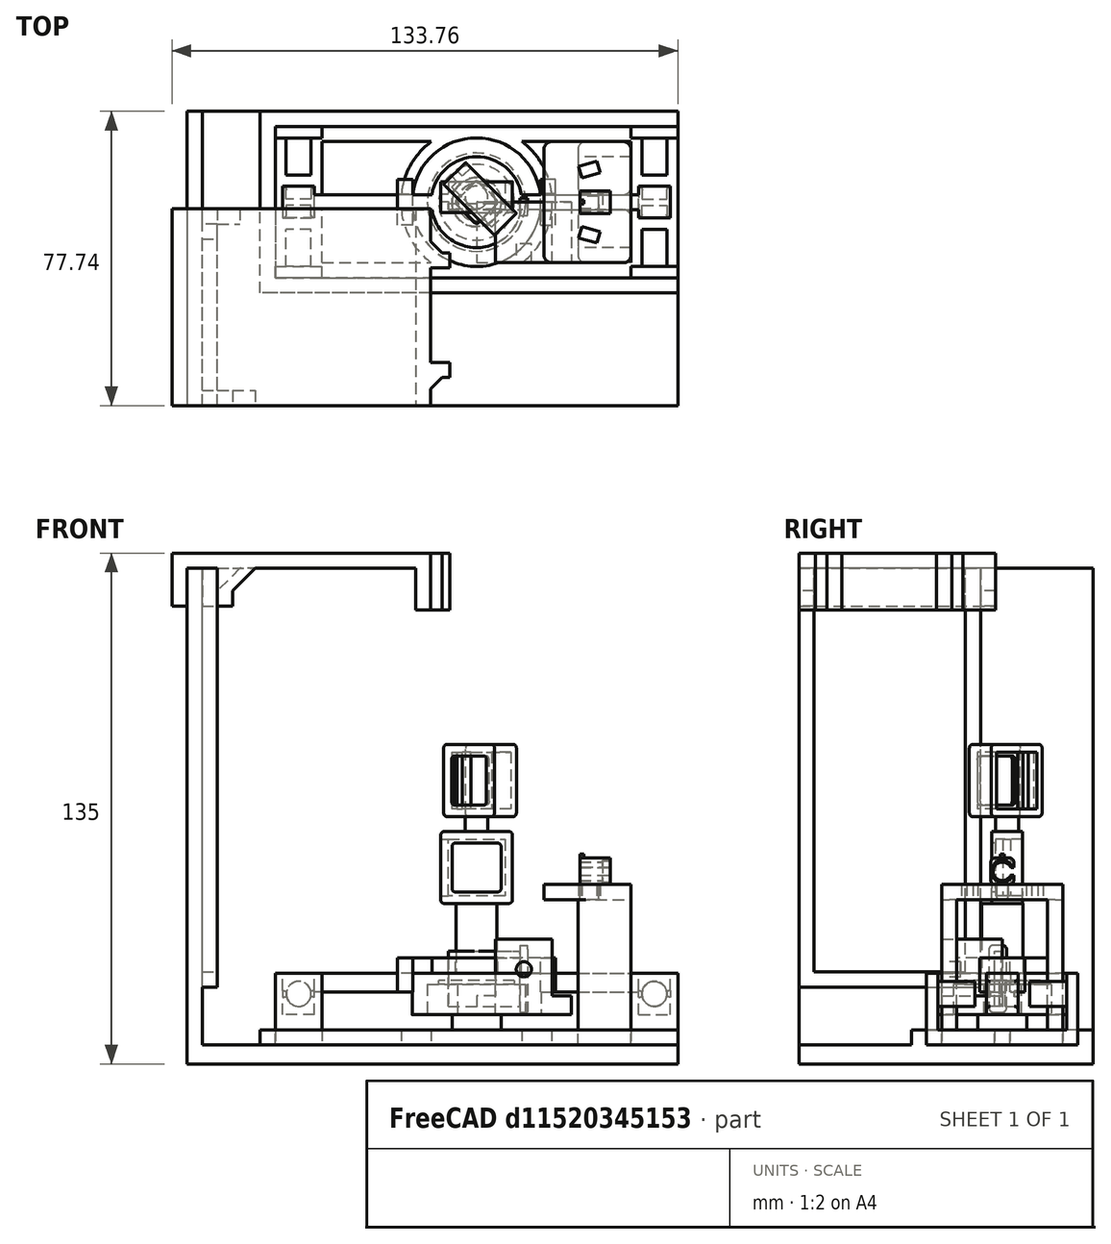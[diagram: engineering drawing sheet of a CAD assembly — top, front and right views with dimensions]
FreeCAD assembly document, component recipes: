
FREECAD ASSEMBLY — COMPONENT RECIPES ("laser2")

This assembly document has 16 components, labeled P0..P15 below (a component is one placed body or linked part). 16 of them carry a construction recipe — the FreeCAD feature program that regenerates the part from scratch, quoted from this document or its linked companion documents; the rest are supplied as boundary geometry only. No exploded tour is included for this assembly.
COMPONENT P0 — recipe-attached ("stator", modeled in this document).
Construction recipe (the document's own serialized feature program — sketch geometry with constraints, then the solid features built on it; lengths are millimeters unless a unit is written):

FEATURE [PartDesign::SubShapeBinder] Binder
  BindCopyOnChange = 0
  BindMode = 0
  ClaimChildren = false
  Context = -> Body [Boolean.Body001.Binder.]
  Fuse = false
  MakeFace = true
  OffsetFill = false
  OffsetIntersection = false
  OffsetJoinType = 0
  OffsetOpenResult = false
  PartialLoad = false
  Refine = true
  Relative = true
  Support = -> [Body002]
  _Version = 2
FEATURE [Sketcher::SketchObject] Sketch001
  ArcFitTolerance = 1e-06
  AttachmentSupport = -> [Origin002]
  ExternalGeometry = -> [Binder]
  ExternalTypes = [0]
  FullyConstrained = true
  MakeInternals = false
  MapMode = 5
  sketch-geometry (1):
    g0: Circle CenterX=0 CenterY=0 CenterZ=0 NormalX=0 NormalY=0 NormalZ=1 AngleXU=0 Radius=5
  constraints (2):
    c: Coincident(g0,g-1)
    c: Equal(g-3,g0)
FEATURE [PartDesign::Pad] Pad
  Direction = (0,0,1)
  Length = 8
  Length2 = 10
  Profile = -> Sketch001
  ReferenceAxis = -> Sketch001 [N_Axis]
  Refine = true
  SideType = 0
  Suppressed = false
  Type = 0
  Type2 = 0
  expr: Length = VarSet.bearing_height
FEATURE [Sketcher::SketchObject] Sketch020
  ArcFitTolerance = 1e-06
  AttachmentSupport = -> [Pad]
  ExternalGeometry = -> [Pad]
  ExternalTypes = [0]
  FullyConstrained = true
  MakeInternals = false
  MapMode = 5
  Placement = pos=(0,0,0) rot=(1,0,0;3.14159rad)
  sketch-geometry (1):
    g0: Circle CenterX=0 CenterY=0 CenterZ=0 NormalX=0 NormalY=0 NormalZ=1 AngleXU=0 Radius=6.5
  constraints (2):
    c: Coincident(g0,g-3)
    c: Distance(g-3,g0) = 1.5
FEATURE [PartDesign::Pad] Pad012
  BaseFeature = -> Pad
  Direction = (0,0,-1)
  Length = 4
  Length2 = 10
  Profile = -> Sketch020
  ReferenceAxis = -> Sketch020 [N_Axis]
  Refine = true
  SideType = 0
  Suppressed = false
  Type = 0
  Type2 = 0
FEATURE [PartDesign::Body] Body001  label="stator"
  AllowCompound = false
  Group = -> [Sketch001,Pad,Binder,Sketch020,Pad012]
  Origin = -> Origin002
  Tip = -> Pad012
COMPONENT P1 — recipe-attached ("mirror_base", modeled in this document).
Construction recipe (the document's own serialized feature program — sketch geometry with constraints, then the solid features built on it; lengths are millimeters unless a unit is written):

FEATURE [PartDesign::SubShapeBinder] Binder006
  BindCopyOnChange = 0
  BindMode = 0
  ClaimChildren = false
  Context = -> Body005 [Binder006.]
  Fuse = false
  MakeFace = true
  OffsetFill = false
  OffsetIntersection = false
  OffsetJoinType = 0
  OffsetOpenResult = false
  PartialLoad = false
  Refine = true
  Relative = true
  Support = -> [Body004]
  _Version = 2
FEATURE [Sketcher::SketchObject] Sketch031
  ArcFitTolerance = 1e-06
  AttachmentSupport = -> [Binder006]
  ExternalGeometry = -> [Binder006]
  ExternalTypes = [0,0,0,0,0,0,0,0]
  FullyConstrained = true
  MakeInternals = false
  MapMode = 5
  Placement = pos=(0,0,11) rot=(1,0,0;3.14159rad)
  sketch-geometry (16):
    g0: ArcOfCircle CenterX=-4.58579 CenterY=1.3e-15 CenterZ=0 NormalX=0 NormalY=0 NormalZ=1 AngleXU=-1.5708 Radius=0.85 StartAngle=3.92699 EndAngle=5.49779
    g1: LineSegment StartX=-5.18683 StartY=-0.601041 StartZ=0 EndX=-0.601041 EndY=-5.18683 EndZ=0
    g2: ArcOfCircle CenterX=-1.2e-15 CenterY=-4.58579 CenterZ=0 NormalX=0 NormalY=0 NormalZ=1 AngleXU=-1.5708 Radius=0.85 StartAngle=5.49779 EndAngle=7.06858
    g3: LineSegment StartX=0.601041 StartY=-5.18683 StartZ=0 EndX=5.18683 EndY=-0.601041 EndZ=0
    g4: ArcOfCircle CenterX=4.58579 CenterY=-7e-16 CenterZ=0 NormalX=0 NormalY=0 NormalZ=1 AngleXU=-1.5708 Radius=0.85 StartAngle=0.785398 EndAngle=2.35619
    g5: LineSegment StartX=5.18683 StartY=0.601041 StartZ=0 EndX=0.601041 EndY=5.18683 EndZ=0
    g6: ArcOfCircle CenterX=3e-16 CenterY=4.58579 CenterZ=0 NormalX=0 NormalY=0 NormalZ=1 AngleXU=-1.5708 Radius=0.85 StartAngle=2.35619 EndAngle=3.92699
    g7: LineSegment StartX=-0.601041 StartY=5.18683 StartZ=0 EndX=-5.18683 EndY=0.601041 EndZ=0
    g8: LineSegment [constr] StartX=5.18683 StartY=0.601041 StartZ=0 EndX=4.58579 EndY=-7e-16 EndZ=0
    g9: LineSegment [constr] StartX=4.58579 StartY=-7e-16 StartZ=0 EndX=5.18683 EndY=-0.601041 EndZ=0
    g10: LineSegment [constr] StartX=0.601041 StartY=5.18683 StartZ=0 EndX=3e-16 EndY=4.58579 EndZ=0
    g11: LineSegment [constr] StartX=3e-16 StartY=4.58579 StartZ=0 EndX=-0.601041 EndY=5.18683 EndZ=0
    g12: LineSegment [constr] StartX=-5.18683 StartY=0.601041 StartZ=0 EndX=-4.58579 EndY=1.3e-15 EndZ=0
    g13: LineSegment [constr] StartX=-4.58579 StartY=1.3e-15 StartZ=0 EndX=-5.18683 EndY=-0.601041 EndZ=0
    g14: LineSegment [constr] StartX=-0.601041 StartY=-5.18683 StartZ=0 EndX=-1.1e-15 EndY=-4.58579 EndZ=0
    g15: LineSegment [constr] StartX=-1.2e-15 StartY=-4.58579 StartZ=0 EndX=0.601041 EndY=-5.18683 EndZ=0
  constraints (33):
    c: Tangent(g0,g1) = -1.5708
    c: Tangent(g0,g7) = -1.5708
    c: Tangent(g1,g2) = -1.5708
    c: Tangent(g2,g3) = -1.5708
    c: Tangent(g3,g4) = -1.5708
    c: Tangent(g4,g5) = -1.5708
    c: Tangent(g5,g6) = -1.5708
    c: Tangent(g6,g7) = -1.5708
    c: Coincident(g8,g4)
    c: Coincident(g8,g4)
    c: Coincident(g9,g4)
    c: Coincident(g9,g3)
    c: Perpendicular(g8,g9)
    c: Coincident(g10,g5)
    c: Coincident(g10,g6)
    c: Coincident(g11,g6)
    c: Coincident(g11,g6)
    c: Distance(g11,g11) = 0.85
    c: Perpendicular(g10,g11)
    c: Coincident(g12,g0)
    c: Coincident(g12,g0)
    c: Coincident(g13,g0)
    c: Coincident(g13,g0)
    c: Perpendicular(g12,g13)
    c: Distance(g12,g12) = 0.85
    c: Coincident(g14,g1)
    c: Coincident(g14,g2)
    c: Coincident(g15,g2)
    c: Coincident(g15,g2)
    c: Distance(g15,g15) = 0.85
    c: Coincident(g0,g-10)
    c: Coincident(g6,g-5)
    c: Coincident(g4,g-6)
FEATURE [PartDesign::Pad] Pad021
  Direction = (0,0,-1)
  Length = 18.4
  Length2 = 10
  Offset = 16
  Profile = -> Sketch031
  ReferenceAxis = -> Sketch031 [N_Axis]
  Refine = true
  Reversed = true
  SideType = 0
  Suppressed = false
  Type = 0
  Type2 = 0
FEATURE [PartDesign::Body] Body005  label="mirror_base"
  AllowCompound = false
  Group = -> [Sketch031,Binder006,Pad021]
  Origin = -> Origin011
  Placement = pos=(0,0,0) rot=(0,0,1;-1.5708rad)
  Tip = -> Pad021
COMPONENT P2 — recipe-attached ("cover", modeled in this document).
Construction recipe (the document's own serialized feature program — sketch geometry with constraints, then the solid features built on it; lengths are millimeters unless a unit is written):

FEATURE [PartDesign::SubShapeBinder] Binder011
  BindCopyOnChange = 0
  BindMode = 0
  ClaimChildren = false
  Context = -> Body006 [Binder011.]
  Fuse = false
  MakeFace = true
  OffsetFill = false
  OffsetIntersection = false
  OffsetJoinType = 0
  OffsetOpenResult = false
  PartialLoad = false
  Refine = true
  Relative = true
  Support = -> [Body008]
  _Version = 2
FEATURE [Sketcher::SketchObject] Sketch036
  ArcFitTolerance = 1e-06
  AttachmentSupport = -> [Binder011]
  ExternalGeometry = -> [Binder011]
  ExternalTypes = [0,0,0,0]
  FullyConstrained = true
  MakeInternals = false
  MapMode = 5
  Placement = pos=(-7.5,0,0) rot=(0.57735,0.57735,0.57735;2.0944rad)
  sketch-geometry (6):
    g0: LineSegment StartX=-1.98579 StartY=16.8 StartZ=0 EndX=-1.98579 EndY=2.2 EndZ=0
    g1: LineSegment StartX=-1.98579 StartY=2.2 StartZ=0 EndX=-0.385786 EndY=2.2 EndZ=0
    g2: LineSegment StartX=-0.385786 StartY=2.2 StartZ=0 EndX=-0.385786 EndY=16.8 EndZ=0
    g3: LineSegment StartX=-0.385786 StartY=16.8 StartZ=0 EndX=-1.98579 EndY=16.8 EndZ=0
    g4: LineSegment [constr] StartX=-0.185786 StartY=2 StartZ=0 EndX=-2.18579 EndY=17 EndZ=0
    g5: GeomPoint [constr] X=-1.18579 Y=9.5 Z=0
  constraints (14):
    c: Coincident(g0,g1)
    c: Coincident(g1,g2)
    c: Coincident(g2,g3)
    c: Coincident(g3,g0)
    c: Vertical(g0)
    c: Vertical(g2)
    c: Horizontal(g1)
    c: Horizontal(g3)
    c: Coincident(g4,g-6)
    c: Coincident(g4,g-4)
    c: Symmetric(g4,g4,g5)
    c: Symmetric(g2,g0,g5)
    c: Distance(g-3,g3) = 0.2
    c: Distance(g-5,g2) = 0.2
FEATURE [PartDesign::Pad] Pad024
  Direction = (1,0,0)
  Length = 10
  Length2 = 10
  Offset = -2
  Profile = -> Sketch036
  ReferenceAxis = -> Sketch036 [N_Axis]
  Refine = true
  SideType = 0
  Suppressed = false
  Type = 3
  Type2 = 0
  UpToFace = -> Binder011 [Face6]
FEATURE [Sketcher::SketchObject] Sketch037
  ArcFitTolerance = 1e-06
  AttachmentSupport = -> [Pad024]
  ExternalGeometry = -> [Pad024]
  ExternalTypes = [0]
  FullyConstrained = true
  MakeInternals = false
  MapMode = 5
  Placement = pos=(11.5,0,0) rot=(0.57735,0.57735,0.57735;2.0944rad)
  sketch-geometry (6):
    g0: LineSegment StartX=-3.48579 StartY=18.3 StartZ=0 EndX=-3.48579 EndY=0.7 EndZ=0
    g1: LineSegment StartX=-3.48579 StartY=0.7 StartZ=0 EndX=1.11421 EndY=0.7 EndZ=0
    g2: LineSegment StartX=1.11421 StartY=0.7 StartZ=0 EndX=1.11421 EndY=18.3 EndZ=0
    g3: LineSegment StartX=1.11421 StartY=18.3 StartZ=0 EndX=-3.48579 EndY=18.3 EndZ=0
    g4: LineSegment [constr] StartX=-1.98579 StartY=16.8 StartZ=0 EndX=-0.385786 EndY=2.2 EndZ=0
    g5: GeomPoint [constr] X=-1.18579 Y=9.5 Z=0
  constraints (14):
    c: Coincident(g0,g1)
    c: Coincident(g1,g2)
    c: Coincident(g2,g3)
    c: Coincident(g3,g0)
    c: Vertical(g0)
    c: Vertical(g2)
    c: Horizontal(g1)
    c: Horizontal(g3)
    c: Coincident(g4,g-6)
    c: Coincident(g4,g-4)
    c: Symmetric(g4,g4,g5)
    c: Symmetric(g0,g2,g5)
    c: Distance(g3,g-5) = 1.5
    c: Distance(g2,g-4) = 1.5
FEATURE [PartDesign::Pad] Pad025
  BaseFeature = -> Pad024
  Direction = (1,0,0)
  Length = 2
  Length2 = 10
  Profile = -> Sketch037
  ReferenceAxis = -> Sketch037 [N_Axis]
  Refine = true
  SideType = 0
  Suppressed = false
  Type = 0
  Type2 = 0
FEATURE [PartDesign::Fillet] Fillet003
  Base = -> Pad025 [Edge17,Edge20,Edge18,Edge22]
  BaseFeature = -> Pad025
  Radius = 1
  Refine = true
  SupportTransform = false
  Suppressed = false
  UseAllEdges = false
FEATURE [PartDesign::Body] Body006  label="cover"
  AllowCompound = false
  Group = -> [Binder011,Sketch036,Pad024,Sketch037,Pad025,Fillet003]
  Origin = -> Origin013
  Tip = -> Fillet003
COMPONENT P3 — recipe-attached ("mirror", modeled in this document).
Construction recipe (the document's own serialized feature program — sketch geometry with constraints, then the solid features built on it; lengths are millimeters unless a unit is written):

FEATURE [Sketcher::SketchObject] Sketch044
  ArcFitTolerance = 1e-06
  AttachmentSupport = -> [Origin019]
  ExternalTypes = [0]
  FullyConstrained = true
  MakeInternals = false
  MapMode = 5
  expr: Constraints[14] = 1 mm + 1.8 mm
  expr: Constraints[8] = VarSet.mirror_width + 2 * 2 mm
  sketch-geometry (7):
    g0: LineSegment StartX=-9.5 StartY=2.8 StartZ=0 EndX=-9.5 EndY=-5.38579 EndZ=0
    g1: LineSegment StartX=-9.5 StartY=-5.38579 StartZ=0 EndX=9.5 EndY=-5.38579 EndZ=0
    g2: LineSegment StartX=9.5 StartY=-5.38579 StartZ=0 EndX=9.5 EndY=2.8 EndZ=0
    g3: LineSegment StartX=9.5 StartY=2.8 StartZ=0 EndX=-9.5 EndY=2.8 EndZ=0
    g4: LineSegment [constr] StartX=-9.5 StartY=-5.38579 StartZ=0 EndX=0 EndY=0 EndZ=0
    g5: LineSegment [constr] StartX=0 StartY=0 StartZ=0 EndX=9.5 EndY=-5.38579 EndZ=0
    g6: GeomPoint [constr] X=0 Y=-5.38579 Z=0
  constraints (18):
    c: Coincident(g0,g1)
    c: Coincident(g1,g2)
    c: Coincident(g2,g3)
    c: Coincident(g3,g0)
    c: Vertical(g0)
    c: Vertical(g2)
    c: Horizontal(g1)
    c: Horizontal(g3)
    c: Distance(g3,g3) = 19
    c: Coincident(g4,g0)
    c: Coincident(g4,g-1)
    c: Coincident(g5,g4)
    c: Coincident(g5,g1)
    c: Equal(g5,g4)
    c: Distance(g4,g3) = 2.8
    c: PointOnObject(g6,g-3)
    c: PointOnObject(g6,g1)
    c: PointOnObject(g6,g-2)
FEATURE [PartDesign::Pad] Pad031
  Direction = (0,0,1)
  Length = 19
  Length2 = 10
  Profile = -> Sketch044
  ReferenceAxis = -> Sketch044 [N_Axis]
  Refine = true
  SideType = 0
  Suppressed = false
  Type = 0
  Type2 = 0
  expr: Length = 2 * 2 mm + VarSet.mirror_width
FEATURE [Sketcher::SketchObject] Sketch045
  ArcFitTolerance = 1e-06
  AttachmentSupport = -> [Pad031]
  ExternalGeometry = -> [Pad031]
  ExternalTypes = [0,0,0,0]
  FullyConstrained = true
  MakeInternals = false
  MapMode = 5
  Placement = pos=(0,-5.38579,0) rot=(1,0,0;1.5708rad)
  sketch-geometry (10):
    g0: LineSegment StartX=-7.5 StartY=17 StartZ=0 EndX=-7.5 EndY=2 EndZ=0
    g1: LineSegment StartX=-7.5 StartY=2 StartZ=0 EndX=7.5 EndY=2 EndZ=0
    g2: LineSegment StartX=7.5 StartY=2 StartZ=0 EndX=7.5 EndY=17 EndZ=0
    g3: LineSegment StartX=7.5 StartY=17 StartZ=0 EndX=-7.5 EndY=17 EndZ=0
    g4: LineSegment StartX=-6.5 StartY=16 StartZ=0 EndX=-6.5 EndY=3 EndZ=0
    g5: LineSegment StartX=-6.5 StartY=3 StartZ=0 EndX=6.5 EndY=3 EndZ=0
    g6: LineSegment StartX=6.5 StartY=3 StartZ=0 EndX=6.5 EndY=16 EndZ=0
    g7: LineSegment StartX=6.5 StartY=16 StartZ=0 EndX=-6.5 EndY=16 EndZ=0
    g8: LineSegment [constr] StartX=9.5 StartY=0 StartZ=0 EndX=-9.5 EndY=19 EndZ=0
    g9: GeomPoint [constr] X=2.45925e-11 Y=9.5 Z=0
  constraints (25):
    c: Coincident(g0,g1)
    c: Coincident(g1,g2)
    c: Coincident(g2,g3)
    c: Coincident(g3,g0)
    c: Vertical(g0)
    c: Vertical(g2)
    c: Horizontal(g1)
    c: Horizontal(g3)
    c: Coincident(g4,g5)
    c: Coincident(g5,g6)
    c: Coincident(g6,g7)
    c: Coincident(g7,g4)
    c: Vertical(g4)
    c: Vertical(g6)
    c: Horizontal(g5)
    c: Horizontal(g7)
    c: Coincident(g8,g-6)
    c: Coincident(g8,g-4)
    c: Symmetric(g8,g8,g9)
    c: Symmetric(g0,g1,g9)
    c: Symmetric(g4,g6,g9)
    c: Distance(g4,g0) = 1
    c: Distance(g-4,g0) = 2
    c: PointOnObject(g0,g8)
    c: PointOnObject(g4,g8)
FEATURE [PartDesign::Pocket] Pocket007
  BaseFeature = -> Pad031
  Direction = (0,1,-2e-16)
  Length = 7.2
  Length2 = 5
  Profile = -> Sketch045 [Edge1,Edge4,Edge3,Edge2]
  ReferenceAxis = -> Sketch045 [N_Axis]
  Refine = true
  SideType = 0
  Suppressed = false
  Type = 0
  Type2 = 0
  expr: Length = 5 mm + 2.2 mm
FEATURE [PartDesign::Pocket] Pocket008
  BaseFeature = -> Pocket007
  Direction = (0,1,-2e-16)
  Length = 5
  Length2 = 5
  Profile = -> Sketch045 [Edge5,Edge8,Edge7,Edge6]
  ReferenceAxis = -> Sketch045 [N_Axis]
  Refine = true
  SideType = 0
  Suppressed = false
  Type = 1
  Type2 = 0
FEATURE [Sketcher::SketchObject] Sketch046
  ArcFitTolerance = 1e-06
  AttachmentSupport = -> [Pocket008]
  ExternalGeometry = -> [Pocket008]
  ExternalTypes = [0]
  FullyConstrained = true
  MakeInternals = false
  MapMode = 5
  Placement = pos=(9.5,0,0) rot=(0.57735,0.57735,0.57735;2.0944rad)
  sketch-geometry (6):
    g0: LineSegment StartX=-0.185786 StartY=17 StartZ=0 EndX=-2.18579 EndY=17 EndZ=0
    g1: LineSegment StartX=-2.18579 StartY=17 StartZ=0 EndX=-2.18579 EndY=2 EndZ=0
    g2: LineSegment StartX=-2.18579 StartY=2 StartZ=0 EndX=-0.185786 EndY=2 EndZ=0
    g3: LineSegment StartX=-0.185786 StartY=17 StartZ=0 EndX=-0.185786 EndY=2 EndZ=0
    g4: LineSegment [constr] StartX=-0.185786 StartY=17 StartZ=0 EndX=1.81421 EndY=17 EndZ=0
    g5: LineSegment [constr] StartX=-0.185786 StartY=2 StartZ=0 EndX=1.81421 EndY=2 EndZ=0
  constraints (16):
    c: Coincident(g0,g1)
    c: Coincident(g1,g2)
    c: Horizontal(g0)
    c: Horizontal(g2)
    c: Vertical(g1)
    c: Distance(g2,g2) = 2
    c: Coincident(g3,g0)
    c: Coincident(g3,g2)
    c: Vertical(g3)
    c: Coincident(g4,g0)
    c: Coincident(g5,g2)
    c: Horizontal(g5)
    c: Horizontal(g4)
    c: Distance(g5,g5) = 2
    c: Coincident(g5,g-3)
    c: Coincident(g4,g-3)
FEATURE [PartDesign::Pocket] Pocket009
  BaseFeature = -> Pocket008
  Direction = (-1,0,0)
  Length = 5
  Length2 = 5
  Profile = -> Sketch046
  ReferenceAxis = -> Sketch046 [N_Axis]
  Refine = true
  SideType = 0
  Suppressed = false
  Type = 2
  Type2 = 0
FEATURE [PartDesign::Fillet] Fillet006
  Base = -> Pocket009 [Edge4,Edge20,Edge19,Edge3,Edge26,Edge27,Edge31,Edge29]
  BaseFeature = -> Pocket009
  Radius = 1
  Refine = true
  SupportTransform = false
  Suppressed = false
  UseAllEdges = false
FEATURE [PartDesign::Body] Body008  label="mirror"
  AllowCompound = false
  Group = -> [Sketch044,Sketch045,Sketch046,Pad031,Pocket007,Pocket008,Pocket009,Fillet006]
  Origin = -> Origin019
  Tip = -> Fillet006
COMPONENT P4 — recipe-attached ("container", modeled in this document).
Construction recipe (the document's own serialized feature program — sketch geometry with constraints, then the solid features built on it; lengths are millimeters unless a unit is written):

FEATURE [PartDesign::SubShapeBinder] Binder014
  BindCopyOnChange = 0
  BindMode = 0
  ClaimChildren = false
  Context = -> Body009 [Binder014.]
  Fuse = false
  MakeFace = true
  OffsetFill = false
  OffsetIntersection = false
  OffsetJoinType = 0
  OffsetOpenResult = false
  PartialLoad = false
  Refine = true
  Relative = true
  Support = -> [Assembly002]
  _Version = 2
FEATURE [Sketcher::SketchObject] Sketch047
  ArcFitTolerance = 1e-06
  AttachmentOffset = pos=(0,0,0) rot=(0,0,1;1.5708rad)
  AttachmentSupport = -> [Binder014]
  ExternalGeometry = -> [Binder014]
  ExternalTypes = [0,0,0,0,0]
  FullyConstrained = true
  MakeInternals = false
  MapMode = 45
  Placement = pos=(1.32e-14,-2.28733e-11,-8) rot=(0,0,1;3.14159rad)
  sketch-geometry (4):
    g0: LineSegment StartX=76.5314 StartY=53.7373 StartZ=0 EndX=-53.2307 EndY=53.7373 EndZ=0
    g1: LineSegment StartX=-53.2307 StartY=53.7373 StartZ=0 EndX=-53.2307 EndY=-24 EndZ=0
    g2: LineSegment StartX=-53.2307 StartY=-24 StartZ=0 EndX=76.5314 EndY=-24 EndZ=0
    g3: LineSegment StartX=76.5314 StartY=-24 StartZ=0 EndX=76.5314 EndY=53.7373 EndZ=0
  constraints (12):
    c: Coincident(g0,g1)
    c: Coincident(g1,g2)
    c: Coincident(g2,g3)
    c: Coincident(g3,g0)
    c: Horizontal(g0)
    c: Horizontal(g2)
    c: Vertical(g1)
    c: Vertical(g3)
    c: Distance(g-5,g0) = 4
    c: Distance(g-5,g3) = 4
    c: PointOnObject(g-7,g1)
    c: Distance(g-7,g1) = 4
FEATURE [PartDesign::Pad] Pad032
  Direction = (0,0,1)
  Length = 5
  Length2 = 10
  Profile = -> Sketch047
  ReferenceAxis = -> Sketch047 [N_Axis]
  Refine = true
  Reversed = true
  SideType = 0
  Suppressed = false
  Type = 0
  Type2 = 0
FEATURE [Sketcher::SketchObject] Sketch048
  ArcFitTolerance = 1e-06
  AttachmentSupport = -> [Pad032]
  ExternalGeometry = -> [Pad032,Binder014]
  ExternalTypes = [0,0]
  FullyConstrained = true
  MakeInternals = false
  MapMode = 5
  Placement = pos=(0,0,-8) rot=(0,0,1;0rad)
  sketch-geometry (4):
    g0: LineSegment StartX=-76.5314 StartY=24 StartZ=0 EndX=-76.5314 EndY=-53.7373 EndZ=0
    g1: LineSegment StartX=-76.5314 StartY=-53.7373 StartZ=0 EndX=-72.5314 EndY=-53.7373 EndZ=0
    g2: LineSegment StartX=-72.5314 StartY=-53.7373 StartZ=0 EndX=-72.5314 EndY=24 EndZ=0
    g3: LineSegment StartX=-72.5314 StartY=24 StartZ=0 EndX=-76.5314 EndY=24 EndZ=0
  constraints (10):
    c: Coincident(g0,g1)
    c: Coincident(g1,g2)
    c: Coincident(g2,g3)
    c: Coincident(g3,g0)
    c: Vertical(g2)
    c: Horizontal(g1)
    c: Horizontal(g3)
    c: Coincident(g0,g-3)
    c: Coincident(g0,g-3)
    c: PointOnObject(g-4,g2)
FEATURE [PartDesign::Pad] Pad033
  BaseFeature = -> Pad032
  Direction = (0,0,1)
  Length = 126
  Length2 = 10
  Profile = -> Sketch048
  ReferenceAxis = -> Sketch048 [N_Axis]
  Refine = true
  SideType = 0
  Suppressed = false
  Type = 0
  Type2 = 0
FEATURE [Sketcher::SketchObject] Sketch049
  ArcFitTolerance = 1e-06
  AttachmentSupport = -> [Pad033]
  ExternalGeometry = -> [Binder014,Pad033]
  ExternalTypes = [0,0,0,0,0]
  FullyConstrained = true
  MakeInternals = false
  MapMode = 5
  Placement = pos=(0,0,-8) rot=(0,0,1;0rad)
  sketch-geometry (8):
    g0: LineSegment StartX=53.2307 StartY=24 StartZ=0 EndX=-57.2307 EndY=24 EndZ=0
    g1: LineSegment StartX=53.2307 StartY=20 StartZ=0 EndX=-53.2307 EndY=20 EndZ=0
    g2: LineSegment StartX=53.2307 StartY=20 StartZ=0 EndX=53.2307 EndY=24 EndZ=0
    g3: LineSegment StartX=-53.2307 StartY=20 StartZ=0 EndX=-53.2307 EndY=-20 EndZ=0
    g4: LineSegment StartX=-53.2307 StartY=-20 StartZ=0 EndX=53.2307 EndY=-20 EndZ=0
    g5: LineSegment StartX=53.2307 StartY=-20 StartZ=0 EndX=53.2307 EndY=-24 EndZ=0
    g6: LineSegment StartX=53.2307 StartY=-24 StartZ=0 EndX=-57.2307 EndY=-24 EndZ=0
    g7: LineSegment StartX=-57.2307 StartY=-24 StartZ=0 EndX=-57.2307 EndY=24 EndZ=0
  constraints (19):
    c: Coincident(g0,g-7)
    c: PointOnObject(g0,g-7)
    c: Coincident(g1,g-5)
    c: Coincident(g1,g-6)
    c: Coincident(g2,g1)
    c: Coincident(g2,g0)
    c: Coincident(g3,g1)
    c: Coincident(g3,g-3)
    c: Coincident(g4,g3)
    c: Coincident(g4,g-4)
    c: Coincident(g5,g4)
    c: Vertical(g5)
    c: Coincident(g6,g5)
    c: Horizontal(g6)
    c: Coincident(g7,g6)
    c: Coincident(g7,g0)
    c: Vertical(g7)
    c: Distance(g1,g7) = 4
    c: Distance(g3,g6) = 4
FEATURE [PartDesign::Pad] Pad034
  BaseFeature = -> Pad033
  Direction = (0,0,1)
  Length = 4
  Length2 = 10
  Profile = -> Sketch049
  ReferenceAxis = -> Sketch049 [N_Axis]
  Refine = true
  SideType = 0
  Suppressed = false
  Type = 0
  Type2 = 0
FEATURE [Sketcher::SketchObject] Sketch050
  ArcFitTolerance = 1e-06
  AttachmentSupport = -> [Pad034]
  ExternalGeometry = -> [Pad034,Binder014]
  ExternalTypes = [0,0,0,0,0]
  FullyConstrained = true
  MakeInternals = false
  MapMode = 5
  Placement = pos=(-72.5314,0,0) rot=(0.57735,0.57735,0.57735;2.0944rad)
  sketch-geometry (10):
    g0: LineSegment [constr] StartX=-49.7373 StartY=117.762 StartZ=0 EndX=-49.7373 EndY=118 EndZ=0
    g1: LineSegment [constr] StartX=-9.73726 StartY=117.762 StartZ=0 EndX=-9.73726 EndY=118 EndZ=0
    g2: LineSegment StartX=-49.7373 StartY=118 StartZ=0 EndX=-53.7373 EndY=118 EndZ=0
    g3: LineSegment StartX=-53.7373 StartY=118 StartZ=0 EndX=-53.7373 EndY=7.30072 EndZ=0
    g4: LineSegment StartX=-49.7373 StartY=11.3007 StartZ=0 EndX=-49.7373 EndY=118 EndZ=0
    g5: LineSegment StartX=-49.7373 StartY=11.3007 StartZ=0 EndX=-9.73726 EndY=11.3007 EndZ=0
    g6: LineSegment StartX=-9.73726 StartY=11.3007 StartZ=0 EndX=-9.73726 EndY=118 EndZ=0
    g7: LineSegment StartX=-53.7373 StartY=7.30072 StartZ=0 EndX=-5.73726 EndY=7.30072 EndZ=0
    g8: LineSegment StartX=-5.73726 StartY=7.30072 StartZ=0 EndX=-5.73726 EndY=118 EndZ=0
    g9: LineSegment StartX=-9.73726 StartY=118 StartZ=0 EndX=-5.73726 EndY=118 EndZ=0
  constraints (25):
    c: Coincident(g0,g-4)
    c: PointOnObject(g0,g-3)
    c: Vertical(g0)
    c: Coincident(g1,g-5)
    c: PointOnObject(g1,g-3)
    c: Vertical(g1)
    c: Coincident(g2,g0)
    c: Coincident(g2,g-3)
    c: Coincident(g3,g2)
    c: Vertical(g3)
    c: Coincident(g4,g-7)
    c: Coincident(g4,g0)
    c: Coincident(g5,g4)
    c: Coincident(g5,g-6)
    c: Coincident(g6,g5)
    c: Coincident(g6,g1)
    c: Coincident(g7,g3)
    c: Horizontal(g7)
    c: Coincident(g8,g7)
    c: PointOnObject(g8,g-3)
    c: Vertical(g8)
    c: Distance(g5,g8) = 4
    c: Distance(g5,g7) = 4
    c: Coincident(g9,g1)
    c: Coincident(g9,g8)
FEATURE [PartDesign::Pad] Pad035
  BaseFeature = -> Pad034
  Direction = (1,0,0)
  Length = 4
  Length2 = 10
  Profile = -> Sketch050
  ReferenceAxis = -> Sketch050 [N_Axis]
  Refine = true
  SideType = 0
  Suppressed = false
  Type = 0
  Type2 = 0
FEATURE [PartDesign::Body] Body009  label="container"
  AllowCompound = false
  Group = -> [Binder014,Sketch047,Pad032,Sketch048,Pad033,Sketch049,Pad034,Sketch050,Pad035]
  Origin = -> Origin021
  Tip = -> Pad035
COMPONENT P5 — recipe-attached ("laser_diode_holder", modeled in this document).
Construction recipe (the document's own serialized feature program — sketch geometry with constraints, then the solid features built on it; lengths are millimeters unless a unit is written):

FEATURE [PartDesign::SubShapeBinder] Binder016
  BindCopyOnChange = 0
  BindMode = 0
  ClaimChildren = false
  Context = -> Body012 [Binder016.]
  Fuse = false
  MakeFace = true
  OffsetFill = false
  OffsetIntersection = false
  OffsetJoinType = 0
  OffsetOpenResult = false
  PartialLoad = false
  Refine = true
  Relative = true
  Support = -> [Body009]
  _Version = 2
FEATURE [PartDesign::SubShapeBinder] Binder017
  BindCopyOnChange = 0
  BindMode = 0
  ClaimChildren = false
  Context = -> Body012 [Binder017.]
  Fuse = false
  MakeFace = true
  OffsetFill = false
  OffsetIntersection = false
  OffsetJoinType = 0
  OffsetOpenResult = false
  PartialLoad = false
  Refine = true
  Relative = true
  Support = -> [Assembly002]
  _Version = 2
FEATURE [Sketcher::SketchObject] Sketch060
  ArcFitTolerance = 1e-06
  AttachmentSupport = -> [Binder016]
  ExternalGeometry = -> [Binder017,Binder016]
  ExternalTypes = [0,0,0,0]
  FullyConstrained = true
  MakeInternals = false
  MapMode = 5
  Placement = pos=(1.726e-13,0,118) rot=(0,0,1;0rad)
  sketch-geometry (4):
    g0: LineSegment StartX=-80.5314 StartY=-53.7373 StartZ=0 EndX=-12.1314 EndY=-53.7373 EndZ=0
    g1: LineSegment StartX=-12.1314 StartY=-53.7373 StartZ=0 EndX=-12.1314 EndY=-1.73726 EndZ=0
    g2: LineSegment StartX=-12.1314 StartY=-1.73726 StartZ=0 EndX=-80.5314 EndY=-1.73726 EndZ=0
    g3: LineSegment StartX=-80.5314 StartY=-1.73726 StartZ=0 EndX=-80.5314 EndY=-53.7373 EndZ=0
  constraints (12):
    c: Horizontal(g0)
    c: Coincident(g1,g0)
    c: Vertical(g1)
    c: Coincident(g2,g1)
    c: Horizontal(g2)
    c: Coincident(g3,g2)
    c: Coincident(g3,g0)
    c: Vertical(g3)
    c: PointOnObject(g-4,g1)
    c: PointOnObject(g-5,g0)
    c: Distance(g-5,g3) = 4
    c: Distance(g-6,g2) = 4
FEATURE [PartDesign::Pad] Pad039
  Direction = (1.5e-15,0,1)
  Length = 4
  Length2 = 10
  Profile = -> Sketch060
  ReferenceAxis = -> Sketch060 [N_Axis]
  Refine = true
  SideType = 0
  Suppressed = false
  Type = 0
  Type2 = 0
FEATURE [Sketcher::SketchObject] Sketch061
  ArcFitTolerance = 1e-06
  AttachmentSupport = -> [Pad039]
  ExternalGeometry = -> [Pad039,Binder016]
  ExternalTypes = [0,0,0,0,0,0,0]
  FullyConstrained = true
  MakeInternals = false
  MapMode = 5
  Placement = pos=(1.716e-13,0,118) rot=(1,0,0;3.14159rad)
  sketch-geometry (12):
    g0: LineSegment StartX=-76.5314 StartY=1.73726 StartZ=0 EndX=-76.5314 EndY=53.7373 EndZ=0
    g1: LineSegment StartX=-76.5314 StartY=53.7373 StartZ=0 EndX=-80.5314 EndY=53.7373 EndZ=0
    g2: LineSegment StartX=-80.5314 StartY=53.7373 StartZ=0 EndX=-80.5314 EndY=1.73726 EndZ=0
    g3: LineSegment StartX=-80.5314 StartY=1.73726 StartZ=0 EndX=-76.5314 EndY=1.73726 EndZ=0
    g4: LineSegment StartX=-72.5314 StartY=5.73726 StartZ=0 EndX=-72.5314 EndY=1.73726 EndZ=0
    g5: LineSegment StartX=-72.5314 StartY=1.73726 StartZ=0 EndX=-68.5314 EndY=1.73726 EndZ=0
    g6: LineSegment StartX=-68.5314 StartY=1.73726 StartZ=0 EndX=-68.5314 EndY=5.73726 EndZ=0
    g7: LineSegment StartX=-68.5314 StartY=5.73726 StartZ=0 EndX=-72.5314 EndY=5.73726 EndZ=0
    g8: LineSegment StartX=-68.5314 StartY=49.7373 StartZ=0 EndX=-64.5314 EndY=49.7373 EndZ=0
    g9: LineSegment StartX=-64.5314 StartY=49.7373 StartZ=0 EndX=-64.5314 EndY=53.7373 EndZ=0
    g10: LineSegment StartX=-64.5314 StartY=53.7373 StartZ=0 EndX=-68.5314 EndY=53.7373 EndZ=0
    g11: LineSegment StartX=-68.5314 StartY=53.7373 StartZ=0 EndX=-68.5314 EndY=49.7373 EndZ=0
  constraints (30):
    c: Coincident(g0,g1)
    c: Coincident(g1,g2)
    c: Coincident(g2,g3)
    c: Coincident(g3,g0)
    c: Vertical(g0)
    c: Horizontal(g3)
    c: Coincident(g4,g5)
    c: Coincident(g5,g6)
    c: Coincident(g6,g7)
    c: Coincident(g7,g4)
    c: Vertical(g4)
    c: Vertical(g6)
    c: Horizontal(g5)
    c: Coincident(g4,g-9)
    c: PointOnObject(g5,g-4)
    c: Coincident(g6,g-9)
    c: Coincident(g8,g9)
    c: Coincident(g9,g10)
    c: Coincident(g10,g11)
    c: Coincident(g11,g8)
    c: Horizontal(g8)
    c: Horizontal(g10)
    c: Vertical(g9)
    c: Vertical(g11)
    c: Distance(g9,g11) = 4
    c: Coincident(g8,g-7)
    c: PointOnObject(g9,g-6)
    c: Coincident(g0,g-5)
    c: Coincident(g1,g-6)
    c: Coincident(g-4,g2)
FEATURE [PartDesign::Pad] Pad040
  BaseFeature = -> Pad039
  Direction = (0,0,-1)
  Length = 10
  Length2 = 10
  Profile = -> Sketch061
  ReferenceAxis = -> Sketch061 [N_Axis]
  Refine = true
  SideType = 0
  Suppressed = false
  Type = 0
  Type2 = 0
FEATURE [Sketcher::SketchObject] Sketch066
  ArcFitTolerance = 1e-06
  AttachmentSupport = -> [Pad040]
  ExternalGeometry = -> [Pad040]
  ExternalTypes = [0,0,0]
  FullyConstrained = true
  MakeInternals = false
  MapMode = 5
  Placement = pos=(1.774e-13,0,122) rot=(0,0,1;0rad)
  sketch-geometry (4):
    g0: LineSegment StartX=-12.1314 StartY=-1.73726 StartZ=0 EndX=-16.1314 EndY=-1.73726 EndZ=0
    g1: LineSegment StartX=-16.1314 StartY=-1.73726 StartZ=0 EndX=-16.1314 EndY=-53.7373 EndZ=0
    g2: LineSegment StartX=-16.1314 StartY=-53.7373 StartZ=0 EndX=-12.1314 EndY=-53.7373 EndZ=0
    g3: LineSegment StartX=-12.1314 StartY=-53.7373 StartZ=0 EndX=-12.1314 EndY=-1.73726 EndZ=0
  constraints (10):
    c: Coincident(g0,g1)
    c: Coincident(g1,g2)
    c: Coincident(g2,g3)
    c: Coincident(g3,g0)
    c: Horizontal(g0)
    c: Horizontal(g2)
    c: Vertical(g1)
    c: Distance(g1,g3) = 4
    c: Coincident(g0,g-4)
    c: Coincident(g-5,g2)
FEATURE [PartDesign::Pad] Pad043
  BaseFeature = -> Pad040
  Direction = (1.5e-15,0,1)
  Length = 15
  Length2 = 10
  Profile = -> Sketch066
  ReferenceAxis = -> Sketch066 [N_Axis]
  Refine = true
  Reversed = true
  SideType = 0
  Suppressed = false
  Type = 0
  Type2 = 0
FEATURE [Sketcher::SketchObject] Sketch067
  ArcFitTolerance = 1e-06
  AttachmentSupport = -> [Pad043]
  ExternalGeometry = -> [Pad043,Binder017]
  ExternalTypes = [0,0,0,0]
  FullyConstrained = true
  MakeInternals = false
  MapMode = 5
  Placement = pos=(-12.1314,0,2.82e-14) rot=(0.57735,0.57735,0.57735;2.0944rad)
  sketch-geometry (8):
    g0: LineSegment StartX=-46.3686 StartY=107 StartZ=0 EndX=-46.3686 EndY=122 EndZ=0
    g1: LineSegment StartX=-46.3686 StartY=122 StartZ=0 EndX=-42.3686 EndY=122 EndZ=0
    g2: LineSegment StartX=-42.3686 StartY=122 StartZ=0 EndX=-42.3686 EndY=107 EndZ=0
    g3: LineSegment StartX=-42.3686 StartY=107 StartZ=0 EndX=-46.3686 EndY=107 EndZ=0
    g4: LineSegment StartX=-13.3686 StartY=107 StartZ=0 EndX=-17.3686 EndY=107 EndZ=0
    g5: LineSegment StartX=-17.3686 StartY=107 StartZ=0 EndX=-17.3686 EndY=122 EndZ=0
    g6: LineSegment StartX=-17.3686 StartY=122 StartZ=0 EndX=-13.3686 EndY=122 EndZ=0
    g7: LineSegment StartX=-13.3686 StartY=122 StartZ=0 EndX=-13.3686 EndY=107 EndZ=0
  constraints (24):
    c: Coincident(g0,g1)
    c: Coincident(g1,g2)
    c: Coincident(g2,g3)
    c: Coincident(g3,g0)
    c: Vertical(g0)
    c: Vertical(g2)
    c: Horizontal(g1)
    c: Horizontal(g3)
    c: PointOnObject(g0,g-3)
    c: PointOnObject(g-4,g2)
    c: Distance(g3,g3) = 4
    c: Coincident(g4,g5)
    c: Coincident(g5,g6)
    c: Coincident(g6,g7)
    c: Coincident(g7,g4)
    c: Horizontal(g4)
    c: Horizontal(g6)
    c: Vertical(g5)
    c: Vertical(g7)
    c: PointOnObject(g4,g-3)
    c: PointOnObject(g-5,g5)
    c: Distance(g4,g4) = 4
    c: PointOnObject(g1,g-6)
    c: PointOnObject(g6,g-6)
FEATURE [PartDesign::Pad] Pad044
  BaseFeature = -> Pad043
  Direction = (1,0,-2.2e-15)
  Length = 5
  Length2 = 10
  Profile = -> Sketch067
  ReferenceAxis = -> Sketch067 [N_Axis]
  Refine = true
  SideType = 0
  Suppressed = false
  Type = 0
  Type2 = 0
FEATURE [PartDesign::Chamfer] Chamfer
  Angle = 45
  Base = -> Pad044 [Edge36,Edge35]
  BaseFeature = -> Pad044
  ChamferType = 0
  FlipDirection = false
  Refine = true
  Size = 6
  Size2 = 1
  SupportTransform = false
  Suppressed = false
  UseAllEdges = false
FEATURE [PartDesign::Chamfer] Chamfer001
  Angle = 45
  Base = -> Chamfer [Edge44,Edge79]
  BaseFeature = -> Chamfer
  ChamferType = 0
  FlipDirection = false
  Refine = true
  Size = 3
  Size2 = 1
  SupportTransform = false
  Suppressed = false
  UseAllEdges = false
FEATURE [PartDesign::Body] Body012  label="laser_diode_holder"
  AllowCompound = false
  Group = -> [Sketch060,Pad039,Sketch061,Pad040,Sketch066,Pad043,Sketch067,Pad044,Binder016,Binder017,Chamfer,Chamfer001]
  Origin = -> Origin027
  Tip = -> Chamfer001
COMPONENT P6 — recipe-attached ("bearing002", modeled in this document).
Construction recipe (the document's own serialized feature program — sketch geometry with constraints, then the solid features built on it; lengths are millimeters unless a unit is written):

FEATURE [Sketcher::SketchObject] Sketch002
  ArcFitTolerance = 1e-06
  AttachmentSupport = -> [Origin004]
  ExternalTypes = [0]
  FullyConstrained = true
  MakeInternals = false
  MapMode = 5
  expr: Constraints[1] = VarSet.bearing_inner_diameter
  expr: Constraints[3] = VarSet.bearing_diameter
  sketch-geometry (2):
    g0: Circle CenterX=0 CenterY=0 CenterZ=0 NormalX=0 NormalY=0 NormalZ=1 AngleXU=0 Radius=5
    g1: Circle CenterX=0 CenterY=0 CenterZ=0 NormalX=0 NormalY=0 NormalZ=1 AngleXU=0 Radius=13
  constraints (4):
    c: Coincident(g0,g-1)
    c: Diameter(g0) = 10
    c: Coincident(g1,g0)
    c: Diameter(g1) = 26
FEATURE [PartDesign::Pad] Pad001
  Direction = (0,0,1)
  Length = 8
  Length2 = 10
  Profile = -> Sketch002
  ReferenceAxis = -> Sketch002 [N_Axis]
  Refine = true
  SideType = 0
  Suppressed = false
  Type = 0
  Type2 = 0
  expr: Length = VarSet.bearing_height
FEATURE [PartDesign::Body] Body002  label="bearing"
  AllowCompound = false
  Group = -> [Sketch002,Pad001]
  Origin = -> Origin004
  Tip = -> Pad001
COMPONENT P7 — recipe-attached ("rotor002", modeled in this document).
Construction recipe (the document's own serialized feature program — sketch geometry with constraints, then the solid features built on it; lengths are millimeters unless a unit is written):

FEATURE [PartDesign::SubShapeBinder] Binder002
  BindCopyOnChange = 0
  BindMode = 0
  ClaimChildren = false
  Context = -> Body003 [Binder002.]
  Fuse = false
  MakeFace = true
  OffsetFill = false
  OffsetIntersection = false
  OffsetJoinType = 0
  OffsetOpenResult = false
  PartialLoad = false
  Refine = true
  Relative = true
  Support = -> [Body002]
  _Version = 2
FEATURE [Sketcher::SketchObject] Sketch006
  ArcFitTolerance = 1e-06
  AttachmentSupport = -> [Origin006]
  ExternalGeometry = -> [Binder002]
  ExternalTypes = [0]
  FullyConstrained = true
  MakeInternals = false
  MapMode = 5
  expr: Constraints[22] = VarSet.magnet_diameter + 2 mm
  expr: Constraints[26] = VarSet.magnet_distance
  expr: Constraints[44] = 2 * VarSet.magnet_height + 2 mm
  expr: Constraints[7] = 180 ° - VarSet.target_angle
  expr: Constraints[8] = 180 ° - VarSet.target_angle
  sketch-geometry (17):
    g0: Circle CenterX=0 CenterY=0 CenterZ=0 NormalX=0 NormalY=0 NormalZ=1 AngleXU=0 Radius=13
    g1: ArcOfCircle CenterX=0 CenterY=0 CenterZ=0 NormalX=0 NormalY=0 NormalZ=1 AngleXU=0 Radius=17 StartAngle=3.25951 EndAngle=6.28319
    g2: LineSegment StartX=-16.8819 StartY=2 StartZ=0 EndX=-42.8307 EndY=2 EndZ=0
    g3: LineSegment StartX=-16.8819 StartY=-2 StartZ=0 EndX=-42.8307 EndY=-2 EndZ=0
    g4: ArcOfCircle CenterX=0 CenterY=0 CenterZ=0 NormalX=0 NormalY=0 NormalZ=1 AngleXU=0 Radius=17 StartAngle=0 EndAngle=3.02367
    g5: LineSegment [constr] StartX=0 StartY=0 StartZ=0 EndX=-51.2307 EndY=7.2 EndZ=0
    g6: LineSegment [constr] StartX=0 StartY=0 StartZ=0 EndX=-51.2307 EndY=-7.2 EndZ=0
    g7: LineSegment StartX=-42.8307 StartY=2 StartZ=0 EndX=-42.8307 EndY=4.2 EndZ=0
    g8: LineSegment StartX=-42.8307 StartY=4.2 StartZ=0 EndX=-51.2307 EndY=4.2 EndZ=0
    g9: LineSegment StartX=-42.8307 StartY=-2 StartZ=0 EndX=-42.8307 EndY=-4.2 EndZ=0
    g10: LineSegment StartX=-42.8307 StartY=-4.2 StartZ=0 EndX=-51.2307 EndY=-4.2 EndZ=0
    g11: LineSegment [constr] StartX=-42.8307 StartY=-2 StartZ=0 EndX=-42.8307 EndY=2 EndZ=0
    g12: LineSegment [constr] StartX=-51.2307 StartY=4.2 StartZ=0 EndX=-51.2307 EndY=7.2 EndZ=0
    g13: LineSegment [constr] StartX=-16.8819 StartY=-2 StartZ=0 EndX=-16.8819 EndY=0 EndZ=0
    g14: LineSegment [constr] StartX=-16.8819 StartY=0 StartZ=0 EndX=-16.8819 EndY=2 EndZ=0
    g15: LineSegment [constr] StartX=-51.2307 StartY=-7.2 StartZ=0 EndX=-51.2307 EndY=-4.2 EndZ=0
    g16: LineSegment StartX=-51.2307 StartY=4.2 StartZ=0 EndX=-51.2307 EndY=-4.2 EndZ=0
  constraints (46):
    c: Coincident(g0,g-3)
    c: Coincident(g1,g0)
    c: Coincident(g2,g4)
    c: Coincident(g3,g1)
    c: Coincident(g1,g4)
    c: Distance(g4,g0) = 4
    c: Coincident(g5,g-1)
    c: Angle(g-1,g5) = 3.00197
    c: Angle(g6,g-1) = 3.00197
    c: Coincident(g6,g5)
    c: Coincident(g4,g1)
    c: PointOnObject(g1,g-1)
    c: Vertical(g7)
    c: Coincident(g8,g7)
    c: Horizontal(g8)
    c: Vertical(g9)
    c: Coincident(g10,g9)
    c: Horizontal(g10)
    c: Coincident(g11,g9)
    c: Coincident(g11,g7)
    c: Vertical(g11)
    c: Equal(g7,g9)
    c: Distance(g8,g8) = 8.4
    c: Coincident(g12,g8)
    c: Coincident(g12,g5)
    c: Vertical(g12)
    c: Distance(g12,g12) = 3
    c: Coincident(g13,g1)
    c: PointOnObject(g13,g-1)
    c: Vertical(g13)
    c: Coincident(g14,g13)
    c: Coincident(g14,g2)
    c: Vertical(g14)
    c: Horizontal(g2)
    c: Coincident(g7,g2)
    c: Horizontal(g3)
    c: Distance(g2,g3) = 4
    c: Coincident(g9,g3)
    c: Coincident(g15,g6)
    c: Coincident(g15,g10)
    c: Vertical(g15)
    c: Coincident(g16,g8)
    c: Coincident(g16,g10)
    c: Vertical(g16)
    c: DistanceY(g16,g16) = 8.4
    c: Equal(g-3,g0)
FEATURE [PartDesign::Pad] Pad004
  Direction = (0,0,1)
  Length = 11
  Length2 = 10
  Profile = -> Sketch006
  ReferenceAxis = -> Sketch006 [N_Axis]
  Refine = true
  SideType = 0
  Suppressed = false
  Type = 0
  Type2 = 0
  expr: Length = VarSet.bearing_height + 3 mm
FEATURE [PartDesign::Mirrored] Mirror001
  MirrorPlane = -> XZ_Plane003
  Refine = true
  Suppressed = false
  TransformMode = 0
FEATURE [Sketcher::SketchObject] Sketch023
  ArcFitTolerance = 1e-06
  AttachmentSupport = -> [Pad004]
  ExternalGeometry = -> [Pad004]
  ExternalTypes = [0]
  FullyConstrained = true
  MakeInternals = false
  MapMode = 5
  Placement = pos=(0,0,11) rot=(0,0,1;0rad)
  sketch-geometry (1):
    g0: Circle CenterX=0 CenterY=0 CenterZ=0 NormalX=0 NormalY=0 NormalZ=1 AngleXU=0 Radius=17
  constraints (2):
    c: Coincident(g0,g-3)
    c: PointOnObject(g-3,g0)
FEATURE [PartDesign::Pad] Pad014
  BaseFeature = -> Pad004
  Direction = (0,0,1)
  Length = 2
  Length2 = 10
  Profile = -> Sketch023
  ReferenceAxis = -> Sketch023 [N_Axis]
  Refine = true
  Reversed = true
  SideType = 0
  Suppressed = false
  Type = 0
  Type2 = 0
FEATURE [Sketcher::SketchObject] Sketch024
  ArcFitTolerance = 1e-06
  AttachmentSupport = -> [Pad014]
  ExternalGeometry = -> [Pad014]
  ExternalTypes = [0]
  FullyConstrained = true
  MakeInternals = false
  MapMode = 5
  Placement = pos=(0,0,9) rot=(1,0,0;3.14159rad)
  sketch-geometry (1):
    g0: Circle CenterX=0 CenterY=0 CenterZ=0 NormalX=0 NormalY=0 NormalZ=1 AngleXU=0 Radius=10
  constraints (2):
    c: Coincident(g0,g-3)
    c: Distance(g-3,g0) = 3
FEATURE [PartDesign::Pad] Pad015
  BaseFeature = -> Pad014
  Direction = (0,0,-1)
  Length = 1
  Length2 = 10
  Profile = -> Sketch024
  ReferenceAxis = -> Sketch024 [N_Axis]
  Refine = true
  SideType = 0
  Suppressed = false
  Type = 0
  Type2 = 0
FEATURE [PartDesign::Mirrored] Mirrored001
  BaseFeature = -> Pad015
  MirrorPlane = -> Sketch006 [V_Axis]
  Originals = -> [Pad004]
  Refine = true
  Suppressed = false
  TransformMode = 0
FEATURE [Sketcher::SketchObject] Sketch008
  ArcFitTolerance = 1e-06
  AttachmentSupport = -> [Mirrored001]
  ExternalGeometry = -> [Pad004]
  ExternalTypes = [0,0,0,0]
  FullyConstrained = true
  MakeInternals = false
  MapMode = 5
  Placement = pos=(0,-4.2,0) rot=(1,0,0;1.5708rad)
  expr: Constraints[2] = VarSet.magnet_diameter + 0.2 mm
  sketch-geometry (3):
    g0: LineSegment [constr] StartX=-51.2307 StartY=0 StartZ=0 EndX=-42.8307 EndY=11 EndZ=0
    g1: GeomPoint [constr] X=-47.0307 Y=5.5 Z=0
    g2: Circle CenterX=-47.0307 CenterY=5.5 CenterZ=0 NormalX=0 NormalY=0 NormalZ=1 AngleXU=0 Radius=3.3
  constraints (5):
    c: Symmetric(g0,g0,g1)
    c: Coincident(g2,g1)
    c: Diameter(g2) = 6.6
    c: Coincident(g0,g-6)
    c: Coincident(g0,g-4)
FEATURE [PartDesign::Pocket] Pocket001
  BaseFeature = -> Mirrored001
  Direction = (0,1,-2e-16)
  Length = 3.4
  Length2 = 5
  Profile = -> Sketch008
  ReferenceAxis = -> Sketch008 [N_Axis]
  Refine = true
  SideType = 0
  Suppressed = false
  Type = 0
  Type2 = 0
  expr: Length = VarSet.magnet_height + 0.2 mm
FEATURE [PartDesign::Mirrored] Mirror
  MirrorPlane = -> Sketch008 [V_Axis]
  Refine = true
  Suppressed = false
  TransformMode = 0
FEATURE [PartDesign::MultiTransform] MultiTransform
  BaseFeature = -> Pocket001
  Originals = -> [Pocket001]
  Refine = true
  Suppressed = false
  TransformMode = 0
  Transformations = -> [Mirror,Mirror001]
FEATURE [Sketcher::SketchObject] Sketch025
  ArcFitTolerance = 1e-06
  AttachmentSupport = -> [MultiTransform]
  ExternalGeometry = -> [MultiTransform]
  ExternalTypes = [0,0]
  FullyConstrained = true
  MakeInternals = false
  MapMode = 5
  Placement = pos=(0,0,0) rot=(1,0,0;3.14159rad)
  sketch-geometry (3):
    g0: GeomPoint X=-16.8819 Y=2 Z=0
    g1: ArcOfCircle CenterX=0 CenterY=-8.526e-13 CenterZ=0 NormalX=0 NormalY=0 NormalZ=1 AngleXU=0 Radius=17 StartAngle=3.02367 EndAngle=3.25951
    g2: LineSegment StartX=-42.8307 StartY=2 StartZ=0 EndX=-42.8307 EndY=-2 EndZ=0
  constraints (6):
    c: Coincident(g2,g-4)
    c: Coincident(g0,g-3)
    c: Coincident(g1,g-4)
    c: Coincident(g1,g0)
    c: Coincident(g2,g-3)
    c: Coincident(g1,g-1)
FEATURE [PartDesign::Pocket] Pocket002
  BaseFeature = -> MultiTransform
  Direction = (0,0,1)
  Length = 6
  Length2 = 5
  Profile = -> Sketch025
  ReferenceAxis = -> Sketch025 [N_Axis]
  Refine = true
  SideType = 0
  Suppressed = false
  Type = 0
  Type2 = 0
FEATURE [PartDesign::Mirrored] Mirrored
  BaseFeature = -> Pocket002
  MirrorPlane = -> Sketch025 [V_Axis]
  Originals = -> [Pocket002]
  Refine = true
  Suppressed = false
  TransformMode = 0
FEATURE [PartDesign::Fillet] Fillet
  Base = -> Mirrored [Edge34,Edge46,Edge41,Edge30]
  BaseFeature = -> Mirrored
  Radius = 1
  Refine = true
  SupportTransform = false
  Suppressed = false
  UseAllEdges = false
FEATURE [PartDesign::Body] Body003  label="rotor"
  AllowCompound = false
  Group = -> [Binder002,Sketch006,Pad004,Pad014,Pad015,Sketch008,Mirrored001,Pocket001,MultiTransform,Mirror,Mirror001,Sketch023,Sketch024,Sketch025,Pocket002,Mirrored,Fillet]
  Origin = -> Origin006
  Tip = -> Fillet
COMPONENT P8 — recipe-attached ("mirror_holder_adapter002", modeled in this document).
Construction recipe (the document's own serialized feature program — sketch geometry with constraints, then the solid features built on it; lengths are millimeters unless a unit is written):

FEATURE [PartDesign::SubShapeBinder] Binder005
  BindCopyOnChange = 0
  BindMode = 0
  ClaimChildren = false
  Context = -> Body004 [Binder005.]
  Fuse = false
  MakeFace = true
  OffsetFill = false
  OffsetIntersection = false
  OffsetJoinType = 0
  OffsetOpenResult = false
  PartialLoad = false
  Refine = true
  Relative = true
  Support = -> [Body003]
  _Version = 2
FEATURE [Sketcher::SketchObject] Sketch028
  ArcFitTolerance = 1e-06
  AttachmentSupport = -> [Binder005]
  ExternalGeometry = -> [Binder005]
  ExternalTypes = [0,0,0,0,0,0,0]
  FullyConstrained = true
  MakeInternals = false
  MapMode = 5
  Placement = pos=(0,0,11) rot=(0,0,1;0rad)
  sketch-geometry (13):
    g0: LineSegment StartX=20.8819 StartY=-6 StartZ=0 EndX=20.8819 EndY=6 EndZ=0
    g1: LineSegment StartX=20.8819 StartY=6 StartZ=0 EndX=16.8819 EndY=6 EndZ=0
    g2: LineSegment StartX=16.8819 StartY=-6 StartZ=0 EndX=20.8819 EndY=-6 EndZ=0
    g3: GeomPoint [constr] X=17 Y=0 Z=0
    g4: LineSegment [constr] StartX=16.8819 StartY=6 StartZ=0 EndX=20.8819 EndY=-6 EndZ=0
    g5: GeomPoint [constr] X=18.8819 Y=0 Z=0
    g6: LineSegment StartX=16.8819 StartY=6 StartZ=0 EndX=16.8819 EndY=2 EndZ=0
    g7: ArcOfCircle CenterX=0 CenterY=0 CenterZ=0 NormalX=0 NormalY=0 NormalZ=1 AngleXU=0 Radius=12 StartAngle=0.167448 EndAngle=6.11574
    g8: LineSegment StartX=16.8819 StartY=2 StartZ=0 EndX=11.8322 EndY=2 EndZ=0
    g9: LineSegment StartX=16.8819 StartY=-2 StartZ=0 EndX=11.8322 EndY=-2 EndZ=0
    g10: LineSegment StartX=16.8819 StartY=-6 StartZ=0 EndX=16.8819 EndY=-2 EndZ=0
    g11: LineSegment StartX=16.8819 StartY=-2 StartZ=0 EndX=16.8819 EndY=-2 EndZ=0
    g12: LineSegment [constr] StartX=16.8819 StartY=2 StartZ=0 EndX=16.8819 EndY=-2 EndZ=0
  constraints (32):
    c: Coincident(g0,g1)
    c: Coincident(g2,g0)
    c: Vertical(g0)
    c: Horizontal(g1)
    c: Horizontal(g2)
    c: Distance(g1,g1) = 4
    c: PointOnObject(g3,g-1)
    c: PointOnObject(g3,g-8)
    c: Distance(g0,g-3) = 4
    c: Coincident(g4,g1)
    c: Coincident(g4,g0)
    c: Symmetric(g4,g4,g5)
    c: PointOnObject(g5,g-1)
    c: Coincident(g6,g1)
    c: Vertical(g6)
    c: Coincident(g7,g-9)
    c: Coincident(g8,g6)
    c: Horizontal(g8)
    c: Coincident(g9,g-9)
    c: Horizontal(g9)
    c: Coincident(g10,g2)
    c: PointOnObject(g10,g-4)
    c: Vertical(g10)
    c: Coincident(g11,g10)
    c: Coincident(g11,g9)
    c: Coincident(g12,g6)
    c: Coincident(g12,g10)
    c: Vertical(g12)
    c: Diameter(g7) = 24
    c: Coincident(g8,g7)
    c: Coincident(g9,g7)
    c: Coincident(g-8,g6)
FEATURE [PartDesign::Pad] Pad019
  Direction = (0,0,1)
  Length = 4
  Length2 = 10
  Profile = -> Sketch028
  ReferenceAxis = -> Sketch028 [N_Axis]
  Refine = true
  SideType = 0
  Suppressed = false
  Type = 0
  Type2 = 0
FEATURE [Sketcher::SketchObject] Sketch029
  ArcFitTolerance = 1e-06
  AttachmentSupport = -> [Pad019]
  ExternalGeometry = -> [Pad019,Binder005]
  ExternalTypes = [0,0,0,0,0,0,0]
  FullyConstrained = true
  MakeInternals = false
  MapMode = 5
  Placement = pos=(0,0,11) rot=(1,0,0;3.14159rad)
  sketch-geometry (8):
    g0: LineSegment StartX=16.8819 StartY=6 StartZ=0 EndX=16.8819 EndY=2.2 EndZ=0
    g1: LineSegment StartX=16.8819 StartY=2.2 StartZ=0 EndX=20.8819 EndY=2.2 EndZ=0
    g2: LineSegment StartX=20.8819 StartY=2.2 StartZ=0 EndX=20.8819 EndY=6 EndZ=0
    g3: LineSegment StartX=20.8819 StartY=6 StartZ=0 EndX=16.8819 EndY=6 EndZ=0
    g4: LineSegment StartX=16.8819 StartY=-6 StartZ=0 EndX=20.8819 EndY=-6 EndZ=0
    g5: LineSegment StartX=20.8819 StartY=-6 StartZ=0 EndX=20.8819 EndY=-2.2 EndZ=0
    g6: LineSegment StartX=20.8819 StartY=-2.2 StartZ=0 EndX=16.8819 EndY=-2.2 EndZ=0
    g7: LineSegment StartX=16.8819 StartY=-2.2 StartZ=0 EndX=16.8819 EndY=-6 EndZ=0
  constraints (22):
    c: PointOnObject(g0,g-5)
    c: PointOnObject(g0,g-5)
    c: Coincident(g1,g0)
    c: PointOnObject(g1,g-3)
    c: Horizontal(g1)
    c: Coincident(g2,g1)
    c: Coincident(g2,g-4)
    c: Coincident(g3,g2)
    c: Coincident(g3,g0)
    c: Horizontal(g3)
    c: Distance(g-8,g1) = 0.2
    c: Coincident(g4,g5)
    c: Coincident(g5,g6)
    c: Coincident(g6,g7)
    c: Coincident(g7,g4)
    c: Horizontal(g4)
    c: Horizontal(g6)
    c: Vertical(g5)
    c: Vertical(g7)
    c: Coincident(g4,g-9)
    c: PointOnObject(g5,g-3)
    c: Distance(g-7,g6) = 0.2
FEATURE [PartDesign::Pad] Pad020
  BaseFeature = -> Pad019
  Direction = (0,0,-1)
  Length = 10
  Length2 = 10
  Profile = -> Sketch029
  ReferenceAxis = -> Sketch029 [N_Axis]
  Refine = true
  SideType = 0
  Suppressed = false
  Type = 3
  Type2 = 0
  UpToFace = -> Binder005 [Face13]
FEATURE [PartDesign::Mirrored] Mirror004
  MirrorPlane = -> Sketch029 [V_Axis]
  Refine = true
  Suppressed = false
  TransformMode = 0
FEATURE [PartDesign::MultiTransform] MultiTransform002
  BaseFeature = -> Pad020
  Originals = -> [Pad020,Pad019]
  Refine = true
  Suppressed = false
  TransformMode = 0
  Transformations = -> [Mirror004]
FEATURE [Sketcher::SketchObject] Sketch030
  ArcFitTolerance = 1e-06
  AttachmentSupport = -> [MultiTransform002]
  ExternalTypes = [0]
  FullyConstrained = true
  MakeInternals = false
  MapMode = 5
  Placement = pos=(0,0,15) rot=(0,0,1;0rad)
  sketch-geometry (12):
    g0: LineSegment StartX=-0.707107 StartY=5.29289 StartZ=0 EndX=-5.29289 EndY=0.707107 EndZ=0
    g1: LineSegment StartX=-5.29289 StartY=-0.707107 StartZ=0 EndX=-0.707107 EndY=-5.29289 EndZ=0
    g2: LineSegment StartX=0.707107 StartY=-5.29289 StartZ=0 EndX=5.29289 EndY=-0.707107 EndZ=0
    g3: LineSegment StartX=5.29289 StartY=0.707107 StartZ=0 EndX=0.707107 EndY=5.29289 EndZ=0
    g4: ArcOfCircle CenterX=-3e-16 CenterY=4.58579 CenterZ=0 NormalX=0 NormalY=0 NormalZ=1 AngleXU=0 Radius=1 StartAngle=0.785398 EndAngle=2.35619
    g5: GeomPoint [constr] X=0 Y=6 Z=0
    g6: ArcOfCircle CenterX=-4.58579 CenterY=6e-16 CenterZ=0 NormalX=0 NormalY=0 NormalZ=1 AngleXU=0 Radius=1 StartAngle=2.35619 EndAngle=3.92699
    g7: GeomPoint [constr] X=-6 Y=0 Z=0
    g8: ArcOfCircle CenterX=-3e-16 CenterY=-4.58579 CenterZ=0 NormalX=0 NormalY=0 NormalZ=1 AngleXU=0 Radius=1 StartAngle=3.92699 EndAngle=5.49779
    g9: GeomPoint [constr] X=0 Y=-6 Z=0
    g10: ArcOfCircle CenterX=4.58579 CenterY=-3e-16 CenterZ=0 NormalX=0 NormalY=0 NormalZ=1 AngleXU=0 Radius=1 StartAngle=5.49779 EndAngle=7.06858
    g11: GeomPoint [constr] X=6 Y=0 Z=0
  constraints (26):
    c: PointOnObject(g5,g-2)
    c: PointOnObject(g7,g-1)
    c: Symmetric(g9,g5,g-1)
    c: Symmetric(g7,g11,g-1)
    c: Distance(g-1,g11) = 6
    c: Distance(g9,g-1) = 6
    c: PointOnObject(g5,g0)
    c: PointOnObject(g5,g3)
    c: Tangent(g0,g4) = -1.5708
    c: Tangent(g3,g4) = -1.5708
    c: PointOnObject(g7,g0)
    c: PointOnObject(g7,g1)
    c: Tangent(g0,g6) = -1.5708
    c: Tangent(g1,g6) = -1.5708
    c: PointOnObject(g9,g1)
    c: PointOnObject(g9,g2)
    c: Tangent(g1,g8) = -1.5708
    c: Tangent(g2,g8) = -1.5708
    c: PointOnObject(g11,g2)
    c: PointOnObject(g11,g3)
    c: Tangent(g2,g10) = -1.5708
    c: Tangent(g3,g10) = -1.5708
    c: Distance(g10,g2) = 1
    c: Distance(g1,g6) = 1
    c: Distance(g1,g8) = 1
    c: Distance(g4,g3) = 1
FEATURE [PartDesign::Pocket] Pocket
  BaseFeature = -> MultiTransform002
  Direction = (0,0,-1)
  Length = 5
  Length2 = 5
  Profile = -> Sketch030
  ReferenceAxis = -> Sketch030 [N_Axis]
  Refine = true
  SideType = 0
  Suppressed = false
  Type = 2
  Type2 = 0
FEATURE [Sketcher::SketchObject] Sketch070
  ArcFitTolerance = 1e-06
  AttachmentSupport = -> [Pocket]
  ExternalGeometry = -> [Pocket]
  ExternalTypes = [0,0,0,0,0,0,0,0]
  FullyConstrained = true
  MakeInternals = false
  MapMode = 5
  Placement = pos=(0,0,15) rot=(0,0,1;0rad)
  sketch-geometry (20):
    g0: ArcOfCircle CenterX=-4.58579 CenterY=7e-16 CenterZ=0 NormalX=0 NormalY=0 NormalZ=1 AngleXU=0 Radius=2 StartAngle=2.35619 EndAngle=3.92699
    g1: LineSegment StartX=-6 StartY=-1.41421 StartZ=0 EndX=-1.41421 EndY=-6 EndZ=0
    g2: ArcOfCircle CenterX=-6e-16 CenterY=-4.58579 CenterZ=0 NormalX=0 NormalY=0 NormalZ=1 AngleXU=0 Radius=2 StartAngle=3.92699 EndAngle=5.49779
    g3: LineSegment StartX=1.41421 StartY=-6 StartZ=0 EndX=6 EndY=-1.41421 EndZ=0
    g4: ArcOfCircle CenterX=4.58579 CenterY=0 CenterZ=0 NormalX=0 NormalY=0 NormalZ=1 AngleXU=0 Radius=2 StartAngle=5.49779 EndAngle=7.06858
    g5: LineSegment StartX=6 StartY=1.41421 StartZ=0 EndX=1.41421 EndY=6 EndZ=0
    g6: ArcOfCircle CenterX=-2.1e-15 CenterY=4.58579 CenterZ=0 NormalX=0 NormalY=0 NormalZ=1 AngleXU=0 Radius=2 StartAngle=0.785398 EndAngle=2.35619
    g7: LineSegment StartX=-1.41421 StartY=6 StartZ=0 EndX=-6 EndY=1.41421 EndZ=0
    g8: LineSegment [constr] StartX=-0.707107 StartY=5.29289 StartZ=0 EndX=-2.1e-15 EndY=4.58579 EndZ=0
    g9: LineSegment [constr] StartX=-2.1e-15 StartY=4.58579 StartZ=0 EndX=0.707107 EndY=5.29289 EndZ=0
    g10: LineSegment [constr] StartX=5.29289 StartY=0.707107 StartZ=0 EndX=4.58579 EndY=0 EndZ=0
    g11: LineSegment [constr] StartX=5.29289 StartY=-0.707107 StartZ=0 EndX=4.58579 EndY=0 EndZ=0
    g12: LineSegment [constr] StartX=0.707107 StartY=-5.29289 StartZ=0 EndX=-6e-16 EndY=-4.58579 EndZ=0
    g13: LineSegment [constr] StartX=-6e-16 StartY=-4.58579 StartZ=0 EndX=-0.707107 EndY=-5.29289 EndZ=0
    g14: LineSegment [constr] StartX=-5.29289 StartY=-0.707107 StartZ=0 EndX=-4.58579 EndY=7e-16 EndZ=0
    g15: LineSegment [constr] StartX=-4.58579 StartY=7e-16 StartZ=0 EndX=-5.29289 EndY=0.707107 EndZ=0
    g16: LineSegment [constr] StartX=5.29289 StartY=0.707107 StartZ=0 EndX=6 EndY=1.41421 EndZ=0
    g17: LineSegment [constr] StartX=5.29289 StartY=-0.707107 StartZ=0 EndX=6 EndY=-1.41421 EndZ=0
    g18: LineSegment [constr] StartX=0.707107 StartY=5.29289 StartZ=0 EndX=1.41421 EndY=6 EndZ=0
    g19: LineSegment [constr] StartX=-0.707107 StartY=5.29289 StartZ=0 EndX=-1.41421 EndY=6 EndZ=0
  constraints (45):
    c: Tangent(g0,g1) = -1.5708
    c: Tangent(g0,g7) = -1.5708
    c: Tangent(g1,g2) = -1.5708
    c: Tangent(g2,g3) = -1.5708
    c: Tangent(g3,g4) = -1.5708
    c: Tangent(g4,g5) = -1.5708
    c: Tangent(g5,g6) = -1.5708
    c: Tangent(g6,g7) = -1.5708
    c: Distance(g-10,g0) = 1
    c: Distance(g0,g-10) = 1
    c: Distance(g-7,g3) = 1
    c: Distance(g-6,g4) = 1
    c: Coincident(g8,g-4)
    c: Coincident(g8,g6)
    c: Coincident(g9,g6)
    c: PointOnObject(g9,g-4)
    c: Coincident(g10,g-6)
    c: Coincident(g10,g4)
    c: Coincident(g11,g-7)
    c: Coincident(g11,g4)
    c: Coincident(g12,g-8)
    c: Coincident(g12,g2)
    c: Coincident(g13,g2)
    c: Coincident(g13,g-9)
    c: Coincident(g14,g-10)
    c: Coincident(g14,g0)
    c: Coincident(g15,g0)
    c: Coincident(g15,g-10)
    c: Equal(g8,g9)
    c: Equal(g9,g10)
    c: Equal(g10,g11)
    c: Equal(g11,g12)
    c: Equal(g12,g13)
    c: Equal(g13,g14)
    c: Coincident(g16,g10)
    c: Coincident(g16,g4)
    c: Coincident(g17,g11)
    c: Coincident(g17,g3)
    c: Parallel(g17,g11)
    c: Coincident(g18,g9)
    c: Coincident(g18,g5)
    c: Coincident(g19,g8)
    c: Coincident(g19,g6)
    c: Parallel(g19,g8)
    c: Parallel(g18,g9)
FEATURE [PartDesign::Pad] Pad045
  BaseFeature = -> Pocket
  Direction = (0,0,1)
  Length = 7
  Length2 = 10
  Profile = -> Sketch070
  ReferenceAxis = -> Sketch070 [N_Axis]
  Refine = true
  SideType = 0
  Suppressed = false
  Type = 0
  Type2 = 0
FEATURE [PartDesign::Body] Body004  label="mirror_holder_adapter"
  AllowCompound = false
  Group = -> [Binder005,Sketch028,Pad019,Sketch029,Pad020,MultiTransform002,Mirror004,Sketch030,Pocket,Sketch070,Pad045]
  Origin = -> Origin009
  Tip = -> Pocket
COMPONENT P9 — recipe-attached ("mirrors002", modeled in this document).
Construction recipe (the document's own serialized feature program — sketch geometry with constraints, then the solid features built on it; lengths are millimeters unless a unit is written):

FEATURE [PartDesign::FeatureBase] Clone005
  BaseFeature = -> Fusion
  Placement = pos=(0,0,0) rot=(0,0,1;4.71239rad)
  Suppressed = false
FEATURE [Sketcher::SketchObject] Sketch068
  ArcFitTolerance = 1e-06
  AttachmentOffset = pos=(0,0,7.5) rot=(0,0,1;0rad)
  AttachmentSupport = -> [Clone005]
  ExternalGeometry = -> [Clone005]
  ExternalTypes = [0,0]
  FullyConstrained = true
  MakeInternals = false
  MapMode = 5
  Placement = pos=(0,0,61.9) rot=(0,0,-1;1.5708rad)
  sketch-geometry (5):
    g0: LineSegment [constr] StartX=-5.43467 StartY=-5.17193 StartZ=0 EndX=5.17193 EndY=5.43467 EndZ=0
    g1: GeomPoint [constr] X=-0.131371 Y=0.131371 Z=0
    g2: LineSegment StartX=-0.131371 StartY=0.131371 StartZ=0 EndX=99.8686 EndY=0.131371 EndZ=0
    g3: LineSegment StartX=-0.131371 StartY=0.131371 StartZ=0 EndX=-0.131371 EndY=-99.8686 EndZ=0
    g4: LineSegment StartX=-0.131371 StartY=0.131371 StartZ=0 EndX=70.5793 EndY=-70.5793 EndZ=0
  constraints (13):
    c: PointOnObject(g0,g-3)
    c: Symmetric(g0,g0,g1)
    c: Coincident(g0,g-4)
    c: Coincident(g2,g1)
    c: Coincident(g3,g1)
    c: Angle(g3,g2) = 1.5708
    c: Parallel(g0,g-4)
    c: DistanceX(g2,g2) = 100
    c: DistanceY(g3,g3) = 100
    c: Angle(g0,g3) = 0.785398
    c: Distance(g4) = 100
    c: Coincident(g4,g1)
    c: Angle(g3,g4) = 0.785398
FEATURE [PartDesign::Body] Body014  label="mirrors_with_points_and_lines"
  AllowCompound = false
  Group = -> [Clone005,Sketch068]
  Origin = -> Origin031
  Tip = -> Clone005
COMPONENT P10 — recipe-attached ("encoder_holder002", modeled in this document).
Construction recipe (the document's own serialized feature program — sketch geometry with constraints, then the solid features built on it; lengths are millimeters unless a unit is written):

FEATURE [PartDesign::SubShapeBinder] Binder010
  BindCopyOnChange = 0
  BindMode = 0
  ClaimChildren = false
  Context = -> Body007 [Binder010.]
  Fuse = false
  MakeFace = true
  OffsetFill = false
  OffsetIntersection = false
  OffsetJoinType = 0
  OffsetOpenResult = false
  PartialLoad = false
  Refine = true
  Relative = true
  Support = -> [Body]
  _Version = 2
FEATURE [Sketcher::SketchObject] Sketch038
  ArcFitTolerance = 1e-06
  AttachmentSupport = -> [Binder010]
  ExternalGeometry = -> [Binder010]
  ExternalTypes = [0,0,0,0,0,0]
  FullyConstrained = true
  MakeInternals = false
  MapMode = 45
  Placement = pos=(1.32e-14,-2.28733e-11,-8) rot=(0,0,1;1.5708rad)
  sketch-geometry (8):
    g0: LineSegment StartX=-16 StartY=-40.8307 StartZ=0 EndX=-2 EndY=-40.8307 EndZ=0
    g1: LineSegment StartX=-2 StartY=-40.8307 StartZ=0 EndX=-2 EndY=-26.8307 EndZ=0
    g2: LineSegment StartX=-2 StartY=-26.8307 StartZ=0 EndX=-16 EndY=-26.8307 EndZ=0
    g3: LineSegment StartX=-16 StartY=-26.8307 StartZ=0 EndX=-16 EndY=-40.8307 EndZ=0
    g4: LineSegment StartX=2 StartY=-40.8307 StartZ=0 EndX=16 EndY=-40.8307 EndZ=0
    g5: LineSegment StartX=16 StartY=-40.8307 StartZ=0 EndX=16 EndY=-26.8307 EndZ=0
    g6: LineSegment StartX=16 StartY=-26.8307 StartZ=0 EndX=2 EndY=-26.8307 EndZ=0
    g7: LineSegment StartX=2 StartY=-26.8307 StartZ=0 EndX=2 EndY=-40.8307 EndZ=0
  constraints (22):
    c: Coincident(g0,g1)
    c: Coincident(g1,g2)
    c: Coincident(g2,g3)
    c: Coincident(g3,g0)
    c: Horizontal(g0)
    c: Horizontal(g2)
    c: Vertical(g1)
    c: Vertical(g3)
    c: Coincident(g0,g-4)
    c: PointOnObject(g1,g-5)
    c: Equal(g3,g0)
    c: Coincident(g4,g5)
    c: Coincident(g5,g6)
    c: Coincident(g6,g7)
    c: Coincident(g7,g4)
    c: Horizontal(g4)
    c: Horizontal(g6)
    c: Vertical(g5)
    c: Vertical(g7)
    c: Coincident(g4,g-7)
    c: PointOnObject(g5,g-8)
    c: Equal(g4,g7)
FEATURE [PartDesign::Pad] Pad026
  Direction = (0,0,1)
  Length = 4
  Length2 = 10
  Profile = -> Sketch038
  ReferenceAxis = -> Sketch038 [N_Axis]
  Refine = true
  SideType = 0
  Suppressed = false
  Type = 0
  Type2 = 0
FEATURE [Sketcher::SketchObject] Sketch039
  ArcFitTolerance = 1e-06
  AttachmentSupport = -> [Pad026]
  ExternalGeometry = -> [Pad026]
  ExternalTypes = [0,0,0,0,0,0,0,0]
  FullyConstrained = true
  MakeInternals = false
  MapMode = 5
  Placement = pos=(0,0,-4) rot=(0,0,1;0rad)
  sketch-geometry (8):
    g0: LineSegment StartX=40.8307 StartY=-16 StartZ=0 EndX=40.8307 EndY=-12 EndZ=0
    g1: LineSegment StartX=40.8307 StartY=-12 StartZ=0 EndX=26.8307 EndY=-12 EndZ=0
    g2: LineSegment StartX=26.8307 StartY=-12 StartZ=0 EndX=26.8307 EndY=-16 EndZ=0
    g3: LineSegment StartX=26.8307 StartY=-16 StartZ=0 EndX=40.8307 EndY=-16 EndZ=0
    g4: LineSegment StartX=26.8307 StartY=12 StartZ=0 EndX=26.8307 EndY=16 EndZ=0
    g5: LineSegment StartX=26.8307 StartY=16 StartZ=0 EndX=40.8307 EndY=16 EndZ=0
    g6: LineSegment StartX=40.8307 StartY=16 StartZ=0 EndX=40.8307 EndY=12 EndZ=0
    g7: LineSegment StartX=40.8307 StartY=12 StartZ=0 EndX=26.8307 EndY=12 EndZ=0
  constraints (20):
    c: Coincident(g0,g1)
    c: Coincident(g1,g2)
    c: Coincident(g2,g3)
    c: Coincident(g3,g0)
    c: Vertical(g0)
    c: Vertical(g2)
    c: Horizontal(g1)
    c: Coincident(g4,g5)
    c: Coincident(g5,g6)
    c: Coincident(g6,g7)
    c: Coincident(g7,g4)
    c: Vertical(g4)
    c: Vertical(g6)
    c: Horizontal(g7)
    c: Equal(g4,g2)
    c: Distance(g2,g2) = 4
    c: Coincident(g4,g-4)
    c: Coincident(g5,g-5)
    c: Coincident(g2,g-10)
    c: Coincident(g0,g-10)
FEATURE [PartDesign::SubShapeBinder] Binder013
  BindCopyOnChange = 0
  BindMode = 0
  ClaimChildren = false
  Context = -> Body007 [Binder013.]
  Fuse = false
  MakeFace = true
  OffsetFill = false
  OffsetIntersection = false
  OffsetJoinType = 0
  OffsetOpenResult = false
  PartialLoad = false
  Refine = true
  Relative = true
  Support = -> [Fusion]
  _Version = 2
FEATURE [PartDesign::Pad] Pad027
  BaseFeature = -> Pad026
  Direction = (0,0,1)
  Length = 10
  Length2 = 10
  Offset = -3
  Profile = -> Sketch039
  ReferenceAxis = -> Sketch039 [N_Axis]
  Refine = true
  SideType = 0
  Suppressed = false
  Type = 3
  Type2 = 0
  UpToFace = -> Binder013 [Face42]
FEATURE [Sketcher::SketchObject] Sketch040
  ArcFitTolerance = 1e-06
  AttachmentSupport = -> [Pad027]
  ExternalGeometry = -> [Pad027]
  ExternalTypes = [0,0,0]
  FullyConstrained = true
  MakeInternals = false
  MapMode = 5
  Placement = pos=(0,12,0) rot=(1,0,0;1.5708rad)
  sketch-geometry (4):
    g0: LineSegment StartX=26.8307 StartY=34.4 StartZ=0 EndX=26.8307 EndY=30.4 EndZ=0
    g1: LineSegment StartX=26.8307 StartY=30.4 StartZ=0 EndX=40.8307 EndY=30.4 EndZ=0
    g2: LineSegment StartX=40.8307 StartY=30.4 StartZ=0 EndX=40.8307 EndY=34.4 EndZ=0
    g3: LineSegment StartX=40.8307 StartY=34.4 StartZ=0 EndX=26.8307 EndY=34.4 EndZ=0
  constraints (10):
    c: Coincident(g0,g1)
    c: Coincident(g1,g2)
    c: Coincident(g2,g3)
    c: Coincident(g3,g0)
    c: Vertical(g0)
    c: Vertical(g2)
    c: Horizontal(g1)
    c: Coincident(g0,g-3)
    c: Distance(g2,g2) = 4
    c: Coincident(g2,g-5)
FEATURE [PartDesign::Pad] Pad028
  BaseFeature = -> Pad027
  Direction = (0,-1,2e-16)
  Length = 10
  Length2 = 10
  Profile = -> Sketch040
  ReferenceAxis = -> Sketch040 [N_Axis]
  Refine = true
  SideType = 0
  Suppressed = false
  Type = 3
  Type2 = 0
  UpToFace = -> Pad027 [Face4]
FEATURE [Sketcher::SketchObject] Sketch041
  ArcFitTolerance = 1e-06
  AttachmentSupport = -> [Pad028]
  ExternalGeometry = -> [Pad028]
  ExternalTypes = [0,0]
  FullyConstrained = true
  MakeInternals = false
  MapMode = 5
  Placement = pos=(26.8307,-2.02e-14,1.92e-14) rot=(0.57735,-0.57735,-0.57735;2.0944rad)
  sketch-geometry (4):
    g0: LineSegment StartX=-16 StartY=34.4 StartZ=0 EndX=-16 EndY=30.4 EndZ=0
    g1: LineSegment StartX=-16 StartY=30.4 StartZ=0 EndX=16 EndY=30.4 EndZ=0
    g2: LineSegment StartX=16 StartY=30.4 StartZ=0 EndX=16 EndY=34.4 EndZ=0
    g3: LineSegment StartX=16 StartY=34.4 StartZ=0 EndX=-16 EndY=34.4 EndZ=0
  constraints (10):
    c: Coincident(g0,g1)
    c: Coincident(g1,g2)
    c: Coincident(g2,g3)
    c: Coincident(g3,g0)
    c: Vertical(g0)
    c: Vertical(g2)
    c: Horizontal(g1)
    c: Coincident(g0,g-4)
    c: PointOnObject(g-3,g1)
    c: Coincident(g2,g-4)
FEATURE [PartDesign::Pad] Pad029
  BaseFeature = -> Pad028
  Direction = (-1,0,0)
  Length = 9
  Length2 = 10
  Profile = -> Sketch041
  ReferenceAxis = -> Sketch041 [N_Axis]
  Refine = true
  SideType = 0
  Suppressed = false
  Type = 0
  Type2 = 0
FEATURE [Sketcher::SketchObject] Sketch042
  ArcFitTolerance = 1e-06
  AttachmentSupport = -> [Pad029]
  ExternalTypes = [0,0]
  FullyConstrained = true
  MakeInternals = false
  MapMode = 5
  Placement = pos=(2.07e-14,0,34.4) rot=(0,0,1;0rad)
  expr: Constraints[4] = 2 * VarSet.target_angle
  expr: Constraints[6] = -2 * VarSet.target_angle
  sketch-geometry (19):
    g0: LineSegment [constr] StartX=-0.185786 StartY=-7.5 StartZ=0 EndX=-0.185786 EndY=7.5 EndZ=0
    g1: GeomPoint [constr] X=-0.185786 Y=5.6875e-12 Z=0
    g2: LineSegment [constr] StartX=-0.185786 StartY=5.6875e-12 StartZ=0 EndX=29.8142 EndY=8.60236 EndZ=0
    g3: LineSegment [constr] StartX=-0.185786 StartY=5.6875e-12 StartZ=0 EndX=29.8142 EndY=-8.60236 EndZ=0
    g4: LineSegment [constr] StartX=-0.185786 StartY=5.6875e-12 StartZ=0 EndX=29.8142 EndY=0 EndZ=0
    g5: LineSegment [constr] StartX=29.8142 StartY=8.60236 StartZ=0 EndX=29.8142 EndY=0 EndZ=0
    g6: LineSegment [constr] StartX=29.8142 StartY=0 StartZ=0 EndX=29.8142 EndY=-8.60236 EndZ=0
    g7: LineSegment StartX=26.9809 StartY=9.41327 StartZ=0 EndX=31.7872 EndY=10.7915 EndZ=0
    g8: LineSegment StartX=31.7872 StartY=10.7915 StartZ=0 EndX=32.6475 EndY=7.79145 EndZ=0
    g9: LineSegment StartX=32.6475 StartY=7.79145 StartZ=0 EndX=27.8412 EndY=6.41327 EndZ=0
    g10: LineSegment StartX=27.8412 StartY=6.41327 StartZ=0 EndX=26.9809 EndY=9.41327 EndZ=0
    g11: LineSegment StartX=27.8412 StartY=-6.41327 StartZ=0 EndX=26.9809 EndY=-9.41327 EndZ=0
    g12: LineSegment StartX=26.9809 StartY=-9.41327 StartZ=0 EndX=31.7872 EndY=-10.7915 EndZ=0
    g13: LineSegment StartX=31.7872 StartY=-10.7915 StartZ=0 EndX=32.6475 EndY=-7.79145 EndZ=0
    g14: LineSegment StartX=32.6475 StartY=-7.79145 StartZ=0 EndX=27.8412 EndY=-6.41327 EndZ=0
    g15: LineSegment StartX=27.3142 StartY=1.56045 StartZ=0 EndX=27.3142 EndY=-1.56045 EndZ=0
    g16: LineSegment StartX=27.3142 StartY=-1.56045 StartZ=0 EndX=32.3142 EndY=-1.56045 EndZ=0
    g17: LineSegment StartX=32.3142 StartY=-1.56045 StartZ=0 EndX=32.3142 EndY=1.56045 EndZ=0
    g18: LineSegment StartX=32.3142 StartY=1.56045 StartZ=0 EndX=27.3142 EndY=1.56045 EndZ=0
  constraints (51):
    c: Coincident(g0,g-3)
    c: PointOnObject(g0,g-4)
    c: Vertical(g0)
    c: Symmetric(g0,g0,g1)
    c: Angle(g-1,g2) = 0.279253
    c: Coincident(g2,g1)
    c: Angle(g-1,g3) = -0.279253
    c: Coincident(g3,g1)
    c: Coincident(g4,g1)
    c: PointOnObject(g4,g-1)
    c: Coincident(g5,g2)
    c: Coincident(g5,g4)
    c: Coincident(g6,g4)
    c: Coincident(g6,g3)
    c: Vertical(g6)
    c: Vertical(g5)
    c: DistanceX(g4,g4) = 30
    c: Coincident(g8,g7)
    c: Coincident(g9,g8)
    c: Coincident(g10,g9)
    c: Coincident(g10,g7)
    c: Perpendicular(g2,g10)
    c: Perpendicular(g2,g8)
    c: Parallel(g7,g2)
    c: Parallel(g9,g2)
    c: Symmetric(g7,g8,g2)
    c: Distance(g7,g7) = 5
    c: DistanceY(g10,g10) = 3
    c: Coincident(g12,g11)
    c: Coincident(g14,g13)
    c: Coincident(g14,g11)
    c: Equal(g10,g11)
    c: Equal(g14,g9)
    c: Equal(g14,g12)
    c: Equal(g13,g11)
    c: Parallel(g3,g12)
    c: Parallel(g3,g14)
    c: Perpendicular(g3,g11)
    c: Perpendicular(g13,g3)
    c: Symmetric(g11,g12,g3)
    c: Coincident(g15,g16)
    c: Coincident(g16,g17)
    c: Coincident(g17,g18)
    c: Coincident(g18,g15)
    c: Vertical(g15)
    c: Vertical(g17)
    c: Horizontal(g16)
    c: Horizontal(g18)
    c: Equal(g9,g18)
    c: Equal(g10,g15)
    c: Symmetric(g15,g16,g4)
FEATURE [PartDesign::Pocket] Pocket006
  BaseFeature = -> Pad029
  Direction = (0,0,-1)
  Length = 5
  Length2 = 5
  Profile = -> Sketch042
  ReferenceAxis = -> Sketch042 [N_Axis]
  Refine = true
  SideType = 0
  Suppressed = false
  Type = 2
  Type2 = 0
FEATURE [PartDesign::Fillet] Fillet004
  Base = -> Pocket006 [Edge20,Edge18,Edge68,Edge67,Edge25,Edge8,Edge2,Edge1,Edge11,Edge47]
  BaseFeature = -> Pocket006
  Radius = 2
  Refine = true
  SupportTransform = false
  Suppressed = false
  UseAllEdges = false
FEATURE [PartDesign::Body] Body007  label="encoder_holder"
  AllowCompound = true
  Group = -> [Binder013,Binder010,Sketch038,Pad026,Sketch039,Pad027,Sketch040,Pad028,Sketch041,Pad029,Sketch042,Pocket006,Fillet004]
  Origin = -> Origin015
  Tip = -> Fillet004
COMPONENT P11 — recipe-attached ("base002", modeled in this document).
Construction recipe (the document's own serialized feature program — sketch geometry with constraints, then the solid features built on it; lengths are millimeters unless a unit is written):

FEATURE [PartDesign::SubShapeBinder] Binder004
  BindCopyOnChange = 0
  BindMode = 0
  ClaimChildren = false
  Context = -> Body [Binder004.]
  Fuse = false
  MakeFace = true
  OffsetFill = false
  OffsetIntersection = false
  OffsetJoinType = 0
  OffsetOpenResult = false
  PartialLoad = false
  Refine = true
  Relative = true
  Support = -> [Body003]
  _Version = 2
FEATURE [Sketcher::SketchObject] Sketch026
  ArcFitTolerance = 1e-06
  AttachmentOffset = pos=(0,0,-4) rot=(0,0,1;0rad)
  AttachmentSupport = -> [Origin]
  ExternalGeometry = -> [Binder004]
  ExternalTypes = [0,0,0,0,0,0,0]
  FullyConstrained = true
  MakeInternals = false
  MapMode = 5
  Placement = pos=(0,0,-4) rot=(0,0,1;0rad)
  sketch-geometry (13):
    g0: LineSegment StartX=-19.8997 StartY=-2 StartZ=0 EndX=-40.8307 EndY=-2 EndZ=0
    g1: LineSegment StartX=-19.8997 StartY=2 StartZ=0 EndX=-40.8307 EndY=2 EndZ=0
    g2: LineSegment StartX=-53.2307 StartY=20 StartZ=0 EndX=-53.2307 EndY=-20 EndZ=0
    g3: LineSegment StartX=-53.2307 StartY=-20 StartZ=0 EndX=-40.8307 EndY=-20 EndZ=0
    g4: LineSegment StartX=-40.8307 StartY=-20 StartZ=0 EndX=-40.8307 EndY=2 EndZ=0
    g5: LineSegment [constr] StartX=-42.8307 StartY=4.2 StartZ=0 EndX=-51.2307 EndY=-4.2 EndZ=0
    g6: GeomPoint [constr] X=-47.0307 Y=-1.81e-14 Z=0
    g7: LineSegment StartX=-40.8307 StartY=-2 StartZ=0 EndX=-40.8307 EndY=16 EndZ=0
    g8: LineSegment [constr] StartX=-40.8307 StartY=-2 StartZ=0 EndX=-40.8307 EndY=2 EndZ=0
    g9: ArcOfCircle CenterX=0 CenterY=0 CenterZ=0 NormalX=0 NormalY=0 NormalZ=1 AngleXU=0 Radius=20 StartAngle=3.24176 EndAngle=7.85398
    g10: LineSegment StartX=-53.2307 StartY=20 StartZ=0 EndX=7.1e-15 EndY=20 EndZ=0
    g11: LineSegment StartX=-40.8307 StartY=16 StartZ=0 EndX=-12 EndY=16 EndZ=0
    g12: ArcOfCircle CenterX=0 CenterY=0 CenterZ=0 NormalX=0 NormalY=0 NormalZ=1 AngleXU=0 Radius=20 StartAngle=2.2143 EndAngle=3.04143
  constraints (34):
    c: Horizontal(g0)
    c: PointOnObject(g1,g-5)
    c: Coincident(g2,g3)
    c: Coincident(g3,g4)
    c: Horizontal(g3)
    c: Vertical(g2)
    c: Coincident(g5,g-9)
    c: Coincident(g5,g-8)
    c: Symmetric(g5,g5,g6)
    c: Symmetric(g3,g2,g6)
    c: Distance(g5,g2) = 2
    c: PointOnObject(g0,g-4)
    c: PointOnObject(g1,g-5)
    c: Vertical(g4)
    c: Coincident(g0,g7)
    c: Coincident(g1,g4)
    c: Coincident(g8,g0)
    c: Coincident(g8,g1)
    c: Vertical(g8)
    c: Distance(g9,g9) = 20
    c: Coincident(g0,g9)
    c: Coincident(g12,g1)
    c: Coincident(g9,g-3)
    c: Horizontal(g11)
    c: PointOnObject(g10,g-2)
    c: Distance(g11,g10) = 4
    c: Coincident(g10,g9)
    c: Coincident(g11,g12)
    c: Coincident(g9,g12)
    c: PointOnObject(g1,g-3)
    c: Vertical(g7)
    c: Coincident(g11,g7)
    c: Coincident(g10,g2)
    c: Horizontal(g10)
FEATURE [PartDesign::Pad] Pad016
  Direction = (0,0,1)
  Length = 4
  Length2 = 10
  Profile = -> Sketch026
  ReferenceAxis = -> Sketch026 [N_Axis]
  Refine = true
  Reversed = true
  SideType = 0
  Suppressed = false
  Type = 0
  Type2 = 0
FEATURE [Sketcher::SketchObject] Sketch
  ArcFitTolerance = 1e-06
  AttachmentSupport = -> [Pad016]
  ExternalGeometry = -> [Binder004,Pad016]
  ExternalTypes = [0,0,0,0]
  FullyConstrained = true
  MakeInternals = false
  MapMode = 5
  Placement = pos=(0,0,-4) rot=(0,0,1;0rad)
  expr: Constraints[2] = VarSet.magnet_distance
  sketch-geometry (6):
    g0: LineSegment [constr] StartX=-51.2307 StartY=4.2 StartZ=0 EndX=-51.2307 EndY=7.2 EndZ=0
    g1: LineSegment StartX=-53.2307 StartY=20 StartZ=0 EndX=-53.2307 EndY=17 EndZ=0
    g2: LineSegment StartX=-53.2307 StartY=17 StartZ=0 EndX=-40.8307 EndY=17 EndZ=0
    g3: LineSegment StartX=-40.8307 StartY=17 StartZ=0 EndX=-40.8307 EndY=20 EndZ=0
    g4: LineSegment StartX=-40.8307 StartY=20 StartZ=0 EndX=-53.2307 EndY=20 EndZ=0
    g5: LineSegment [constr] StartX=-40.8307 StartY=16 StartZ=0 EndX=-40.8307 EndY=17 EndZ=0
  constraints (16):
    c: Coincident(g0,g-3)
    c: Vertical(g0)
    c: DistanceY(g0,g0) = 3
    c: Coincident(g1,g2)
    c: Coincident(g2,g3)
    c: Coincident(g3,g4)
    c: Coincident(g4,g1)
    c: Vertical(g1)
    c: Vertical(g3)
    c: Horizontal(g2)
    c: Horizontal(g4)
    c: Distance(g1,g1) = 3
    c: Coincident(g1,g-5)
    c: Coincident(g5,g-6)
    c: Coincident(g5,g2)
    c: Vertical(g5)
FEATURE [PartDesign::Pad] Pad017
  BaseFeature = -> Pad016
  Direction = (0,0,1)
  Length = 13
  Length2 = 10
  Profile = -> Sketch
  ReferenceAxis = -> Sketch [N_Axis]
  Refine = true
  SideType = 0
  Suppressed = false
  Type = 3
  Type2 = 0
  UpToFace = -> Binder004 [Face9]
FEATURE [Sketcher::SketchObject] Sketch027
  ArcFitTolerance = 1e-06
  AttachmentSupport = -> [Pad017]
  ExternalGeometry = -> [Binder004]
  ExternalTypes = [0]
  FullyConstrained = true
  MakeInternals = false
  MapMode = 5
  Placement = pos=(0,17,0) rot=(1,0,0;1.5708rad)
FEATURE [PartDesign::Pad] Pad018
  BaseFeature = -> Pad017
  Direction = (0,-1,2e-16)
  Length = 10
  Length2 = 10
  Offset = 3
  Profile = -> Sketch027
  ReferenceAxis = -> Sketch027 [N_Axis]
  Refine = true
  SideType = 0
  Suppressed = false
  Type = 3
  Type2 = 0
  UpToFace = -> Binder004 [Face12]
  expr: Offset = VarSet.magnet_distance
FEATURE [PartDesign::Mirrored] Mirror002
  MirrorPlane = -> Sketch027 [V_Axis]
  Refine = true
  Suppressed = false
  TransformMode = 0
FEATURE [PartDesign::Mirrored] Mirror003
  MirrorPlane = -> XZ_Plane
  Refine = true
  Suppressed = false
  TransformMode = 0
FEATURE [PartDesign::MultiTransform] MultiTransform001
  BaseFeature = -> Pad018
  Originals = -> [Pad016,Pad017,Pad018]
  Refine = true
  Suppressed = false
  TransformMode = 0
  Transformations = -> [Mirror002,Mirror003]
FEATURE [PartDesign::Boolean] Boolean
  BaseFeature = -> MultiTransform001
  Group = -> [Body001]
  Refine = true
  Suppressed = false
  Type = 0
FEATURE [PartDesign::Body] Body  label="base"
  AllowCompound = true
  Group = -> [Binder004,Sketch026,Pad016,Sketch,Pad017,Sketch027,Pad018,MultiTransform001,Mirror002,Mirror003,Boolean]
  Origin = -> Origin
  Tip = -> Boolean
COMPONENT P12 — recipe-attached ("rgb_holder001", modeled in this document).
Construction recipe (the document's own serialized feature program — sketch geometry with constraints, then the solid features built on it; lengths are millimeters unless a unit is written):

FEATURE [PartDesign::SubShapeBinder] Binder015
  BindCopyOnChange = 0
  BindMode = 0
  ClaimChildren = false
  Context = -> Body010 [Binder015.]
  Fuse = false
  MakeFace = true
  OffsetFill = false
  OffsetIntersection = false
  OffsetJoinType = 0
  OffsetOpenResult = false
  PartialLoad = false
  Refine = true
  Relative = true
  Support = -> [Body007]
  _Version = 2
FEATURE [Sketcher::SketchObject] Sketch051
  ArcFitTolerance = 1e-06
  AttachmentSupport = -> [Binder015]
  ExternalGeometry = -> [Binder015]
  ExternalTypes = [0,0,0,0]
  FullyConstrained = true
  MakeInternals = false
  MapMode = 5
  Placement = pos=(0,0,30.4) rot=(1,0,0;3.14159rad)
  sketch-geometry (5):
    g0: LineSegment StartX=27.3142 StartY=-1.56045 StartZ=0 EndX=27.3142 EndY=1.56045 EndZ=0
    g1: LineSegment StartX=27.3142 StartY=1.56045 StartZ=0 EndX=32.3142 EndY=1.56045 EndZ=0
    g2: LineSegment StartX=32.3142 StartY=-1.56045 StartZ=0 EndX=27.3142 EndY=-1.56045 EndZ=0
    g3: LineSegment [constr] StartX=27.3142 StartY=-1.56045 StartZ=0 EndX=32.3142 EndY=1.56045 EndZ=0
    g4: LineSegment StartX=32.3142 StartY=1.56045 StartZ=0 EndX=32.3142 EndY=-1.56045 EndZ=0
  constraints (11):
    c: Coincident(g0,g1)
    c: Coincident(g2,g0)
    c: Horizontal(g1)
    c: Coincident(g3,g-4)
    c: Coincident(g3,g-6)
    c: Coincident(g4,g1)
    c: Coincident(g4,g2)
    c: Vertical(g4)
    c: Coincident(g0,g-6)
    c: Coincident(g0,g3)
    c: Coincident(g2,g-5)
FEATURE [PartDesign::Pad] Pad036
  Direction = (0,0,-1)
  Length = 10
  Length2 = 10
  Profile = -> Sketch051
  ReferenceAxis = -> Sketch051 [N_Axis]
  Refine = true
  SideType = 0
  Suppressed = false
  Type = 3
  Type2 = 0
  UpToFace = -> Binder015 [Face15]
FEATURE [Sketcher::SketchObject] Sketch052
  ArcFitTolerance = 1e-06
  AttachmentSupport = -> [Pad036]
  ExternalGeometry = -> [Pad036]
  ExternalTypes = [0,0]
  FullyConstrained = true
  MakeInternals = false
  MapMode = 5
  Placement = pos=(2.07e-14,0,34.4) rot=(0,0,1;0rad)
  sketch-geometry (6):
    g0: LineSegment StartX=27.3142 StartY=3 StartZ=0 EndX=27.3142 EndY=-3 EndZ=0
    g1: LineSegment StartX=27.3142 StartY=-3 StartZ=0 EndX=35.3142 EndY=-3 EndZ=0
    g2: LineSegment StartX=35.3142 StartY=-3 StartZ=0 EndX=35.3142 EndY=3 EndZ=0
    g3: LineSegment StartX=35.3142 StartY=3 StartZ=0 EndX=27.3142 EndY=3 EndZ=0
    g4: LineSegment [constr] StartX=27.3142 StartY=1.56045 StartZ=0 EndX=27.3142 EndY=3 EndZ=0
    g5: LineSegment [constr] StartX=27.3142 StartY=-1.56045 StartZ=0 EndX=27.3142 EndY=-3 EndZ=0
  constraints (16):
    c: Coincident(g0,g1)
    c: Coincident(g1,g2)
    c: Coincident(g2,g3)
    c: Coincident(g3,g0)
    c: Vertical(g0)
    c: Vertical(g2)
    c: Horizontal(g1)
    c: Horizontal(g3)
    c: PointOnObject(g-3,g0)
    c: Coincident(g4,g-3)
    c: Coincident(g4,g0)
    c: Coincident(g5,g-3)
    c: Coincident(g5,g0)
    c: Equal(g4,g5)
    c: Distance(g0,g0) = 6
    c: DistanceX(g3,g3) = 8
FEATURE [PartDesign::Pad] Pad037
  BaseFeature = -> Pad036
  Direction = (0,0,1)
  Length = 7
  Length2 = 10
  Profile = -> Sketch052
  ReferenceAxis = -> Sketch052 [N_Axis]
  Refine = true
  SideType = 0
  Suppressed = false
  Type = 0
  Type2 = 0
FEATURE [Sketcher::SketchObject] Sketch053
  ArcFitTolerance = 1e-06
  AttachmentSupport = -> [Pad037]
  ExternalGeometry = -> [Pad037]
  ExternalTypes = [0,0,0,0]
  FullyConstrained = true
  MakeInternals = false
  MapMode = 5
  Placement = pos=(35.3142,0,0) rot=(0.57735,0.57735,0.57735;2.0944rad)
  sketch-geometry (3):
    g0: LineSegment [constr] StartX=3 StartY=34.4 StartZ=0 EndX=-3 EndY=41.4 EndZ=0
    g1: GeomPoint [constr] X=1.99296e-11 Y=37.9 Z=0
    g2: Circle CenterX=1.99296e-11 CenterY=37.9 CenterZ=0 NormalX=0 NormalY=0 NormalZ=1 AngleXU=0 Radius=2.775
  constraints (5):
    c: Coincident(g0,g-5)
    c: Coincident(g0,g-6)
    c: Symmetric(g0,g0,g1)
    c: Diameter(g2) = 5.55
    c: Coincident(g2,g1)
FEATURE [PartDesign::Pocket] Pocket010
  BaseFeature = -> Pad037
  Direction = (-1,0,0)
  Length = 2
  Length2 = 5
  Profile = -> Sketch053
  ReferenceAxis = -> Sketch053 [N_Axis]
  Refine = true
  SideType = 0
  Suppressed = false
  Type = 0
  Type2 = 0
FEATURE [Sketcher::SketchObject] Sketch054
  ArcFitTolerance = 1e-06
  AttachmentSupport = -> [Pocket010]
  ExternalGeometry = -> [Pocket010]
  ExternalTypes = [0]
  FullyConstrained = true
  MakeInternals = false
  MapMode = 5
  Placement = pos=(33.3142,0,0) rot=(0.57735,0.57735,0.57735;2.0944rad)
  sketch-geometry (1):
    g0: Circle CenterX=0 CenterY=37.9 CenterZ=0 NormalX=0 NormalY=0 NormalZ=1 AngleXU=0 Radius=2.45
  constraints (2):
    c: Diameter(g0) = 4.9
    c: Coincident(g0,g-3)
FEATURE [PartDesign::Pocket] Pocket011
  BaseFeature = -> Pocket010
  Direction = (-1,0,0)
  Length = 5
  Length2 = 5
  Profile = -> Sketch054
  ReferenceAxis = -> Sketch054 [N_Axis]
  Refine = true
  SideType = 0
  Suppressed = false
  Type = 1
  Type2 = 0
FEATURE [PartDesign::Fillet] Fillet008
  Base = -> Pocket011 [Edge22,Edge24,Edge20,Edge18,Edge4,Edge2]
  BaseFeature = -> Pocket011
  Radius = 1
  Refine = true
  SupportTransform = false
  Suppressed = false
  UseAllEdges = false
FEATURE [Sketcher::SketchObject] Sketch057
  ArcFitTolerance = 1e-06
  AttachmentSupport = -> [Pocket011]
  ExternalGeometry = -> [Pocket011]
  ExternalTypes = [0,0,0]
  FullyConstrained = false
  MakeInternals = false
  MapMode = 5
  Placement = pos=(35.3142,0,0) rot=(0.57735,0.57735,0.57735;2.0944rad)
  sketch-geometry (10):
    g0: LineSegment [constr] StartX=3 StartY=34.4 StartZ=0 EndX=-3 EndY=41.4 EndZ=0
    g1: GeomPoint [constr] X=1.99294e-11 Y=37.9 Z=0
    g2: LineSegment StartX=4.04081 StartY=38.9 StartZ=0 EndX=1.95919 EndY=38.9 EndZ=0
    g3: LineSegment StartX=1.95919 StartY=38.9 StartZ=0 EndX=1.95919 EndY=36.9 EndZ=0
    g4: LineSegment StartX=1.95919 StartY=36.9 StartZ=0 EndX=4.04081 EndY=36.9 EndZ=0
    g5: LineSegment StartX=4.04081 StartY=36.9 StartZ=0 EndX=4.04081 EndY=38.9 EndZ=0
    g6: GeomPoint X=1.95919 Y=37.9 Z=0
    g7: LineSegment [constr] StartX=1.95919 StartY=37.9 StartZ=0 EndX=1.99294e-11 EndY=37.9 EndZ=0
    g8: LineSegment [constr] StartX=4.04081 StartY=38.9 StartZ=0 EndX=3 EndY=41.4 EndZ=0
    g9: LineSegment [constr] StartX=1.95919 StartY=38.9 StartZ=0 EndX=3 EndY=41.4 EndZ=0
  constraints (21):
    c: Coincident(g0,g-4)
    c: Coincident(g0,g-3)
    c: Symmetric(g0,g0,g1)
    c: Coincident(g2,g3)
    c: Coincident(g3,g4)
    c: Coincident(g4,g5)
    c: Coincident(g5,g2)
    c: Horizontal(g2)
    c: Horizontal(g4)
    c: Vertical(g3)
    c: Vertical(g5)
    c: Distance(g2,g4) = 2
    c: Symmetric(g3,g3,g6)
    c: Coincident(g7,g6)
    c: Coincident(g7,g1)
    c: Horizontal(g7)
    c: Coincident(g8,g2)
    c: Coincident(g8,g-5)
    c: Coincident(g9,g2)
    c: Coincident(g9,g8)
    c: Equal(g8,g9)
FEATURE [PartDesign::Pocket] Pocket014
  BaseFeature = -> Fillet008
  Direction = (-1,0,0)
  Length = 5
  Length2 = 5
  Profile = -> Sketch057
  ReferenceAxis = -> Sketch057 [N_Axis]
  Refine = true
  SideType = 0
  Suppressed = false
  Type = 1
  Type2 = 0
FEATURE [PartDesign::Body] Body010  label="rgb_holder"
  AllowCompound = false
  Group = -> [Binder015,Sketch051,Pad036,Sketch052,Pad037,Sketch053,Pocket010,Sketch054,Pocket011,Fillet008,Sketch057,Pocket014]
  Origin = -> Origin023
  Tip = -> Pocket014
COMPONENT P13 — recipe-attached ("photodiode_holder001", modeled in this document).
Construction recipe (the document's own serialized feature program — sketch geometry with constraints, then the solid features built on it; lengths are millimeters unless a unit is written):

FEATURE [PartDesign::FeatureBase] Clone
  BaseFeature = -> Pad037
  Suppressed = false
FEATURE [Sketcher::SketchObject] Sketch055
  ArcFitTolerance = 1e-06
  AttachmentSupport = -> [Clone]
  ExternalGeometry = -> [Clone]
  ExternalTypes = [0,0,0,0]
  FullyConstrained = true
  MakeInternals = false
  MapMode = 5
  Placement = pos=(35.3142,0,0) rot=(0.57735,0.57735,0.57735;2.0944rad)
  sketch-geometry (3):
    g0: LineSegment [constr] StartX=3 StartY=34.4 StartZ=0 EndX=-3 EndY=41.4 EndZ=0
    g1: Circle CenterX=1.99299e-11 CenterY=37.9 CenterZ=0 NormalX=0 NormalY=0 NormalZ=1 AngleXU=0 Radius=2.9
    g2: GeomPoint X=1.99299e-11 Y=37.9 Z=0
  constraints (5):
    c: Coincident(g0,g-6)
    c: Coincident(g0,g-4)
    c: Diameter(g1) = 5.8
    c: Symmetric(g0,g0,g2)
    c: Coincident(g1,g2)
FEATURE [PartDesign::Pocket] Pocket012
  BaseFeature = -> Clone
  Direction = (-1,0,0)
  Length = 2
  Length2 = 5
  Profile = -> Sketch055
  ReferenceAxis = -> Sketch055 [N_Axis]
  Refine = true
  SideType = 0
  Suppressed = false
  Type = 0
  Type2 = 0
FEATURE [Sketcher::SketchObject] Sketch056
  ArcFitTolerance = 1e-06
  AttachmentSupport = -> [Pocket012]
  ExternalGeometry = -> [Pocket012]
  ExternalTypes = [0]
  FullyConstrained = true
  MakeInternals = false
  MapMode = 5
  Placement = pos=(33.3142,0,0) rot=(0.57735,0.57735,0.57735;2.0944rad)
  sketch-geometry (1):
    g0: Circle CenterX=0 CenterY=37.9 CenterZ=0 NormalX=0 NormalY=0 NormalZ=1 AngleXU=0 Radius=2.5
  constraints (2):
    c: Diameter(g0) = 5
    c: Coincident(g0,g-3)
FEATURE [PartDesign::Pocket] Pocket013
  BaseFeature = -> Pocket012
  Direction = (-1,0,0)
  Length = 5
  Length2 = 5
  Profile = -> Sketch056
  ReferenceAxis = -> Sketch056 [N_Axis]
  Refine = true
  SideType = 0
  Suppressed = false
  Type = 1
  Type2 = 0
FEATURE [PartDesign::Fillet] Fillet009
  Base = -> Pocket013 [Edge22,Edge24,Edge18,Edge20,Edge2,Edge4]
  BaseFeature = -> Pocket013
  Radius = 1
  Refine = true
  SupportTransform = false
  Suppressed = false
  UseAllEdges = false
FEATURE [Sketcher::SketchObject] Sketch058
  ArcFitTolerance = 1e-06
  AttachmentSupport = -> [Pocket013]
  ExternalGeometry = -> [Pocket013]
  ExternalTypes = [0,0,0,0]
  FullyConstrained = false
  MakeInternals = false
  MapMode = 5
  Placement = pos=(35.3142,0,0) rot=(0.57735,0.57735,0.57735;2.0944rad)
  sketch-geometry (8):
    g0: LineSegment [constr] StartX=3 StartY=34.4 StartZ=0 EndX=-3 EndY=41.4 EndZ=0
    g1: GeomPoint [constr] X=1.99295e-11 Y=37.9 Z=0
    g2: GeomPoint [constr] X=3 Y=37.9 Z=0
    g3: LineSegment StartX=1.81397 StartY=36.9 StartZ=0 EndX=4.18603 EndY=36.9 EndZ=0
    g4: LineSegment StartX=4.18603 StartY=36.9 StartZ=0 EndX=4.18603 EndY=38.9 EndZ=0
    g5: LineSegment StartX=4.18603 StartY=38.9 StartZ=0 EndX=1.81397 EndY=38.9 EndZ=0
    g6: LineSegment StartX=1.81397 StartY=38.9 StartZ=0 EndX=1.81397 EndY=36.9 EndZ=0
    g7: GeomPoint [constr] X=3 Y=37.9 Z=0
  constraints (15):
    c: Coincident(g0,g-6)
    c: Coincident(g0,g-4)
    c: Symmetric(g0,g0,g1)
    c: Symmetric(g-6,g-6,g2)
    c: Coincident(g3,g4)
    c: Coincident(g4,g5)
    c: Coincident(g5,g6)
    c: Coincident(g6,g3)
    c: Horizontal(g3)
    c: Horizontal(g5)
    c: Vertical(g4)
    c: Vertical(g6)
    c: Symmetric(g5,g3,g7)
    c: Distance(g3,g5) = 2
    c: Coincident(g7,g2)
FEATURE [PartDesign::Pocket] Pocket015
  BaseFeature = -> Fillet009
  Direction = (-1,0,0)
  Length = 5
  Length2 = 5
  Profile = -> Sketch058
  ReferenceAxis = -> Sketch058 [N_Axis]
  Refine = true
  SideType = 0
  Suppressed = false
  Type = 1
  Type2 = 0
FEATURE [Sketcher::SketchObject] Sketch059
  ArcFitTolerance = 1e-06
  AttachmentSupport = -> [Pocket015]
  ExternalGeometry = -> [Pocket015]
  ExternalTypes = [0,0,0,0]
  FullyConstrained = true
  MakeInternals = false
  MapMode = 5
  Placement = pos=(0,0,41.4) rot=(0,0,1;0rad)
  sketch-geometry (7):
    g0: LineSegment StartX=27.3142 StartY=-0.5 StartZ=0 EndX=27.3142 EndY=0.5 EndZ=0
    g1: LineSegment StartX=27.3142 StartY=0.5 StartZ=0 EndX=28.3142 EndY=0.5 EndZ=0
    g2: LineSegment StartX=28.3142 StartY=0.5 StartZ=0 EndX=28.3142 EndY=-0.5 EndZ=0
    g3: LineSegment StartX=28.3142 StartY=-0.5 StartZ=0 EndX=27.3142 EndY=-0.5 EndZ=0
    g4: LineSegment [constr] StartX=35.3142 StartY=-2 StartZ=0 EndX=27.3142 EndY=2 EndZ=0
    g5: LineSegment [constr] StartX=27.3142 StartY=2 StartZ=0 EndX=27.3142 EndY=-2 EndZ=0
    g6: GeomPoint [constr] X=27.3142 Y=3.08695e-11 Z=0
  constraints (16):
    c: Coincident(g0,g1)
    c: Coincident(g1,g2)
    c: Coincident(g2,g3)
    c: Coincident(g3,g0)
    c: Vertical(g0)
    c: Vertical(g2)
    c: Horizontal(g1)
    c: Horizontal(g3)
    c: Coincident(g4,g-6)
    c: Coincident(g4,g-5)
    c: DistanceX(g1,g1) = 1
    c: DistanceY(g2,g2) = 1
    c: Coincident(g5,g4)
    c: Coincident(g5,g-6)
    c: Symmetric(g5,g5,g6)
    c: Symmetric(g0,g0,g6)
FEATURE [PartDesign::Pad] Pad038
  BaseFeature = -> Pocket015
  Direction = (0,0,1)
  Length = 1
  Length2 = 10
  Profile = -> Sketch059
  ReferenceAxis = -> Sketch059 [N_Axis]
  Refine = true
  SideType = 0
  Suppressed = false
  Type = 0
  Type2 = 0
FEATURE [PartDesign::Body] Body011  label="photodiode_holder"
  AllowCompound = false
  Group = -> [Clone,Sketch055,Pocket012,Sketch056,Pocket013,Fillet009,Sketch058,Pocket015,Sketch059,Pad038]
  Origin = -> Origin025
  Tip = -> Pad038
COMPONENT P14 — same part as P13; its construction recipe is shown at P13.
COMPONENT P15 — recipe-attached ("laser_diode001", modeled in this document).
Construction recipe (the document's own serialized feature program — sketch geometry with constraints, then the solid features built on it; lengths are millimeters unless a unit is written):

FEATURE [Sketcher::SketchObject] Sketch063
  ArcFitTolerance = 1e-06
  AttachmentSupport = -> [Origin029]
  ExternalTypes = [0]
  FullyConstrained = true
  MakeInternals = false
  MapMode = 5
  Placement = pos=(0,0,0) rot=(1,0,0;1.5708rad)
  sketch-geometry (4):
    g0: LineSegment StartX=0 StartY=0 StartZ=0 EndX=25 EndY=0 EndZ=0
    g1: LineSegment StartX=25 StartY=0 StartZ=0 EndX=25 EndY=20 EndZ=0
    g2: LineSegment StartX=25 StartY=20 StartZ=0 EndX=0 EndY=20 EndZ=0
    g3: LineSegment StartX=0 StartY=20 StartZ=0 EndX=0 EndY=0 EndZ=0
  constraints (11):
    c: Coincident(g0,g1)
    c: Coincident(g1,g2)
    c: Coincident(g2,g3)
    c: Coincident(g3,g0)
    c: Horizontal(g0)
    c: Horizontal(g2)
    c: Vertical(g1)
    c: Vertical(g3)
    c: Distance(g1,g3) = 25
    c: Distance(g0,g2) = 20
    c: Coincident(g0,g-1)
FEATURE [PartDesign::Pad] Pad042
  Direction = (0,-1,2e-16)
  Length = 16
  Length2 = 10
  Profile = -> Sketch063
  ReferenceAxis = -> Sketch063 [N_Axis]
  Refine = true
  SideType = 0
  Suppressed = false
  Type = 0
  Type2 = 0
FEATURE [Sketcher::SketchObject] Sketch064
  ArcFitTolerance = 1e-06
  AttachmentSupport = -> [Pad042]
  ExternalGeometry = -> [Pad042]
  ExternalTypes = [0]
  FullyConstrained = true
  MakeInternals = false
  MapMode = 5
  Placement = pos=(0,-16,0) rot=(1,0,0;1.5708rad)
  sketch-geometry (5):
    g0: GeomPoint [constr] X=12.5 Y=3.6e-15 Z=0
    g1: LineSegment [constr] StartX=12.5 StartY=3.6e-15 StartZ=0 EndX=12.5 EndY=10 EndZ=0
    g2: Circle CenterX=12.5 CenterY=12 CenterZ=0 NormalX=0 NormalY=0 NormalZ=1 AngleXU=0 Radius=2
    g3: LineSegment [constr] StartX=12.5 StartY=10 StartZ=0 EndX=12.5 EndY=12 EndZ=0
    g4: GeomPoint [constr] X=12.5 Y=12 Z=0
  constraints (10):
    c: Symmetric(g-3,g-3,g0)
    c: Distance(g1) = 10
    c: Angle(g-1,g1) = 1.5708
    c: Coincident(g1,g0)
    c: Diameter(g2) = 4
    c: PointOnObject(g1,g2)
    c: Coincident(g3,g1)
    c: Coincident(g3,g2)
    c: Vertical(g3)
    c: Coincident(g4,g2)
FEATURE [PartDesign::Pocket] Pocket016
  BaseFeature = -> Pad042
  Direction = (0,1,-2e-16)
  Length = 5
  Length2 = 5
  Profile = -> Sketch064
  ReferenceAxis = -> Sketch064 [N_Axis]
  Refine = true
  SideType = 0
  Suppressed = false
  Type = 0
  Type2 = 0
FEATURE [Sketcher::SketchObject] Sketch065
  ArcFitTolerance = 1e-06
  AttachmentSupport = -> [Pocket016]
  ExternalGeometry = -> [Pocket016]
  ExternalTypes = [0,0,0]
  FullyConstrained = true
  MakeInternals = false
  MapMode = 5
  Placement = pos=(0,-16,0) rot=(1,0,0;1.5708rad)
  sketch-geometry (12):
    g0: LineSegment [constr] StartX=25 StartY=9e-16 StartZ=0 EndX=20 EndY=9e-16 EndZ=0
    g1: LineSegment [constr] StartX=20 StartY=9e-16 StartZ=0 EndX=20 EndY=5 EndZ=0
    g2: LineSegment StartX=20 StartY=5 StartZ=0 EndX=25 EndY=5 EndZ=0
    g3: LineSegment StartX=25 StartY=5 StartZ=0 EndX=25 EndY=20 EndZ=0
    g4: LineSegment StartX=25 StartY=20 StartZ=0 EndX=20 EndY=20 EndZ=0
    g5: LineSegment StartX=20 StartY=20 StartZ=0 EndX=20 EndY=5 EndZ=0
    g6: LineSegment [constr] StartX=0 StartY=9e-16 StartZ=0 EndX=5 EndY=9e-16 EndZ=0
    g7: LineSegment [constr] StartX=5 StartY=9e-16 StartZ=0 EndX=5 EndY=5 EndZ=0
    g8: LineSegment StartX=5 StartY=5 StartZ=0 EndX=5 EndY=20 EndZ=0
    g9: LineSegment StartX=5 StartY=20 StartZ=0 EndX=0 EndY=20 EndZ=0
    g10: LineSegment StartX=0 StartY=20 StartZ=0 EndX=0 EndY=5 EndZ=0
    g11: LineSegment StartX=0 StartY=5 StartZ=0 EndX=5 EndY=5 EndZ=0
  constraints (32):
    c: Distance(g0) = 5
    c: Coincident(g0,g-5)
    c: PointOnObject(g0,g-4)
    c: Distance(g1) = 5
    c: Angle(g-1,g1) = 1.5708
    c: Coincident(g1,g0)
    c: Coincident(g2,g3)
    c: Coincident(g3,g4)
    c: Coincident(g4,g5)
    c: Coincident(g5,g2)
    c: Horizontal(g2)
    c: Horizontal(g4)
    c: Vertical(g3)
    c: Vertical(g5)
    c: Coincident(g2,g1)
    c: Coincident(g3,g-5)
    c: Distance(g6) = 5
    c: Coincident(g6,g-4)
    c: PointOnObject(g6,g-4)
    c: Distance(g7) = 5
    c: Angle(g-1,g7) = 1.5708
    c: Coincident(g7,g6)
    c: Coincident(g8,g9)
    c: Coincident(g9,g10)
    c: Coincident(g10,g11)
    c: Coincident(g11,g8)
    c: Vertical(g8)
    c: Vertical(g10)
    c: Horizontal(g9)
    c: Horizontal(g11)
    c: Coincident(g8,g7)
    c: Coincident(g9,g-3)
FEATURE [PartDesign::Pocket] Pocket017
  BaseFeature = -> Pocket016
  Direction = (0,1,-2e-16)
  Length = 5
  Length2 = 5
  Profile = -> Sketch065
  ReferenceAxis = -> Sketch065 [N_Axis]
  Refine = true
  SideType = 0
  Suppressed = false
  Type = 1
  Type2 = 0
FEATURE [Sketcher::SketchObject] Sketch069
  ArcFitTolerance = 1e-06
  AttachmentSupport = -> [Pocket017]
  ExternalGeometry = -> [Pocket017]
  ExternalTypes = [0]
  FullyConstrained = true
  MakeInternals = false
  MapMode = 5
  Placement = pos=(0,-16,0) rot=(1,0,0;1.5708rad)
  sketch-geometry (1):
    g0: GeomPoint X=12.5 Y=12 Z=0
  constraints (1):
    c: Coincident(g0,g-3)
FEATURE [PartDesign::Body] Body013  label="laser_diode"
  AllowCompound = false
  Group = -> [Sketch063,Pad042,Sketch064,Pocket016,Sketch065,Pocket017,Sketch069]
  Origin = -> Origin029
  Tip = -> Pocket017
PROVENANCE & LICENSES
A FreeCAD (.FCStd) document from a public repository crawl; recipes are the document's own serialized feature recipes (and, for linked parts, companion documents' recipes).
License: as declared in the source repository (recorded in the dataset sidecar).
